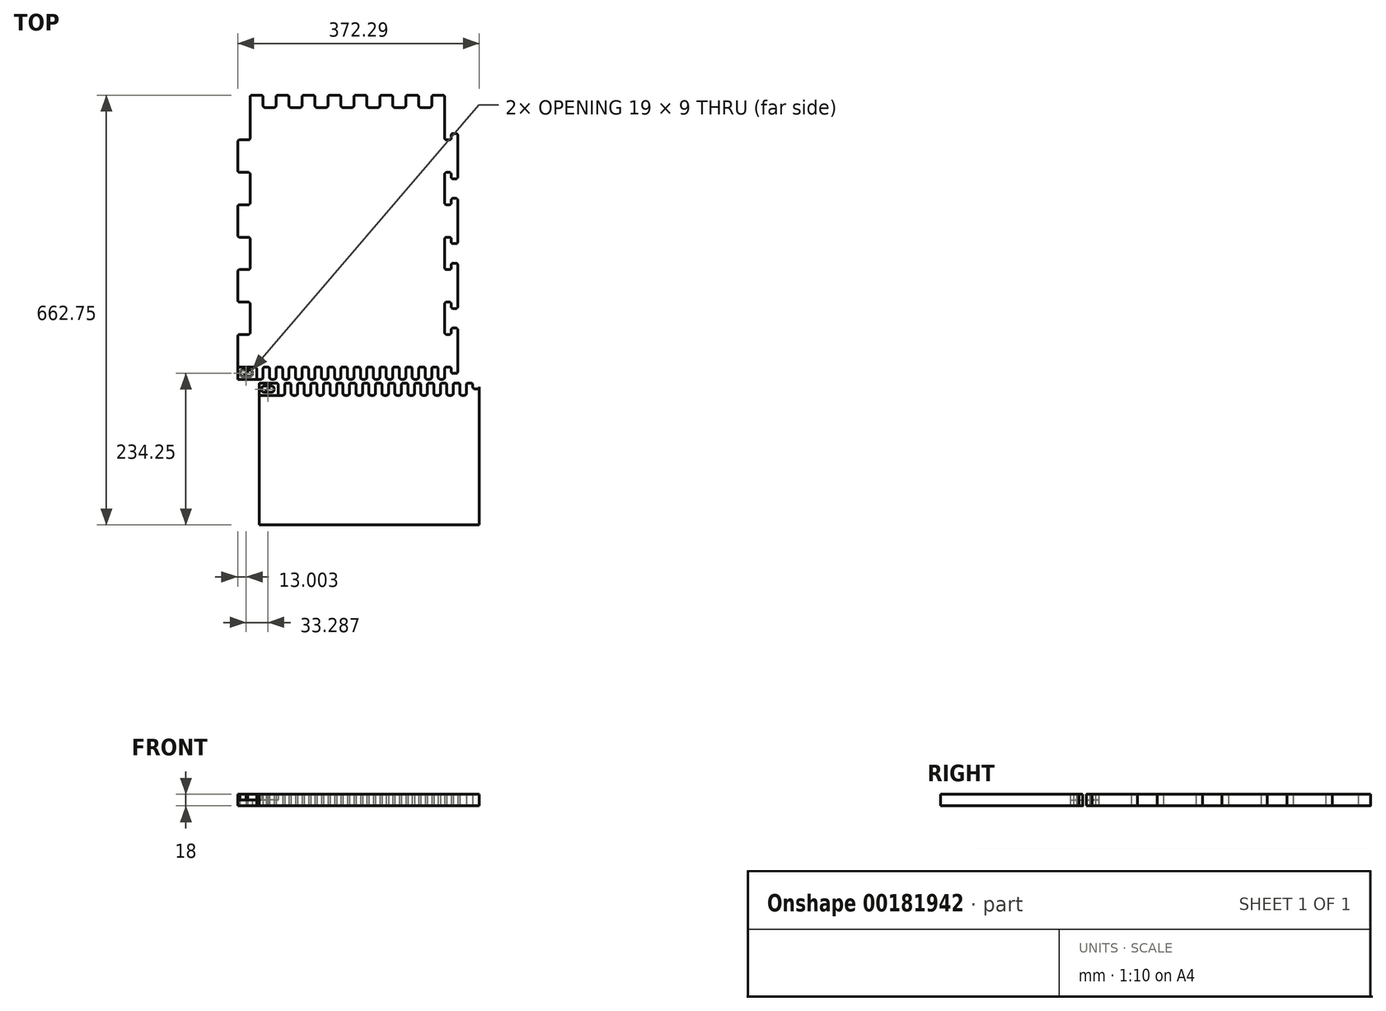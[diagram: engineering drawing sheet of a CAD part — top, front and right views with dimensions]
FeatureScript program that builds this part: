
annotation { "Feature Type Name" : "Feature", "Feature Type Description" : "" }
export const myFeature = defineFeature(function(context is Context, id is Id, definition is map)
    precondition{}
    {
        {
            var Q0;
            Q0=qCreatedBy(makeId("Top.planeOp"),FACE);
            var sketch = newSketch(context, id + "F0", { "sketchPlane" : qUnion([Q0])});
            skLineSegment(sketch, "E0.bottom", {"start": v(0, 0) * mm, "end": v(2000, 0) * mm, "construction": true});
            skLineSegment(sketch, "E0.top", {"start": v(0, 1000) * mm, "end": v(2000, 1000) * mm, "construction": true});
            skLineSegment(sketch, "E0.left", {"start": v(0, 0) * mm, "end": v(0, 1000) * mm, "construction": true});
            skLineSegment(sketch, "E0.right", {"start": v(2000, 0) * mm, "end": v(2000, 1000) * mm, "construction": true});
            skSolve(sketch);
        }
        {
            var Q0;
            Q0=qCreatedBy(makeId("Top.planeOp"),FACE);
            var sketch = newSketch(context, id + "F1", { "sketchPlane" : qUnion([Q0])});
            skLineSegment(sketch, "E1.bottom", {"start": v(5, 5) * mm, "end": v(1995, 5) * mm, "construction": true});
            skLineSegment(sketch, "E1.top", {"start": v(5, 995) * mm, "end": v(1995, 995) * mm, "construction": true});
            skLineSegment(sketch, "E1.left", {"start": v(5, 5) * mm, "end": v(5, 995) * mm, "construction": true});
            skLineSegment(sketch, "E1.right", {"start": v(1995, 5) * mm, "end": v(1995, 995) * mm, "construction": true});
            skPoint(sketch, "E2", {"position": v(0, 0) * mm});
            skPoint(sketch, "E3", {"position": v(5, 5) * mm});
            skSolve(sketch);
        }
        {
            var Q0;
            Q0=qCreatedBy(makeId("Top.planeOp"),FACE);
            var sketch = newSketch(context, id + "F2", { "sketchPlane" : qUnion([Q0])});
            skLineSegment(sketch, "E4.left", {"start": v(301.71, 681.75) * mm, "end": v(301.71, 728.75) * mm});
            skLineSegment(sketch, "E4.right", {"start": v(601.71, 681.75) * mm, "end": v(601.71, 728.75) * mm});
            skLineSegment(sketch, "E5.bottom", {"start": v(301.71, 728.75) * mm, "end": v(321.71, 728.75) * mm, "construction": true});
            skLineSegment(sketch, "E5.top", {"start": v(304.71, 747.75) * mm, "end": v(318.71, 747.75) * mm});
            skLineSegment(sketch, "E5.left", {"start": v(301.71, 728.75) * mm, "end": v(301.71, 744.75) * mm});
            skLineSegment(sketch, "E5.right", {"start": v(321.71, 731.75) * mm, "end": v(321.71, 744.75) * mm});
            skLineSegment(sketch, "E6.bottom", {"start": v(298.71, 678.75) * mm, "end": v(285.71, 678.75) * mm});
            skLineSegment(sketch, "E6.top", {"start": v(298.71, 628.75) * mm, "end": v(285.71, 628.75) * mm});
            skLineSegment(sketch, "E6.left", {"start": v(301.71, 678.75) * mm, "end": v(301.71, 628.75) * mm});
            skLineSegment(sketch, "E6.right", {"start": v(282.71, 675.75) * mm, "end": v(282.71, 631.75) * mm});
            skLineSegment(sketch, "E7.bottom", {"start": v(314.71, 309.75) * mm, "end": v(318.71, 309.75) * mm});
            skLineSegment(sketch, "E8.bottom", {"start": v(604.71, 678.75) * mm, "end": v(608.71, 678.75) * mm});
            skLineSegment(sketch, "E8.top", {"start": v(604.71, 628.75) * mm, "end": v(608.71, 628.75) * mm});
            skLineSegment(sketch, "E8.left", {"start": v(601.71, 678.75) * mm, "end": v(601.71, 628.75) * mm});
            skLineSegment(sketch, "E8.right", {"start": v(621.71, 678.75) * mm, "end": v(621.71, 628.75) * mm});
            skLineSegment(sketch, "E9.bottom", {"start": v(621.71, 678.75) * mm, "end": v(611.71, 678.75) * mm});
            skLineSegment(sketch, "E9.top", {"start": v(618.71, 688.75) * mm, "end": v(614.71, 688.75) * mm});
            skLineSegment(sketch, "E9.left", {"start": v(621.71, 678.75) * mm, "end": v(621.71, 685.75) * mm});
            skLineSegment(sketch, "E9.right", {"start": v(611.71, 681.75) * mm, "end": v(611.71, 685.75) * mm});
            skLineSegment(sketch, "E10.bottom", {"start": v(621.71, 628.75) * mm, "end": v(611.71, 628.75) * mm});
            skLineSegment(sketch, "E10.top", {"start": v(618.71, 618.75) * mm, "end": v(614.71, 618.75) * mm});
            skLineSegment(sketch, "E10.left", {"start": v(621.71, 628.75) * mm, "end": v(621.71, 621.75) * mm});
            skLineSegment(sketch, "E10.right", {"start": v(611.71, 625.75) * mm, "end": v(611.71, 621.75) * mm});
            skPoint(sketch, "E11.visualSharp", {"position": v(611.71, 688.75) * mm});
            skArc(sketch, "E11.filletArc", {"start": v(614.71, 688.75) * mm, "mid": v(612.6, 687.87) * mm, "end": v(611.71, 685.75) * mm});
            skPoint(sketch, "E12.visualSharp", {"position": v(621.71, 688.75) * mm});
            skArc(sketch, "E12.filletArc", {"start": v(621.71, 685.75) * mm, "mid": v(620.83, 687.87) * mm, "end": v(618.71, 688.75) * mm});
            skPoint(sketch, "E13.visualSharp", {"position": v(621.71, 618.75) * mm});
            skArc(sketch, "E13.filletArc", {"start": v(618.71, 618.75) * mm, "mid": v(620.83, 619.63) * mm, "end": v(621.71, 621.75) * mm});
            skPoint(sketch, "E14.visualSharp", {"position": v(611.71, 618.75) * mm});
            skArc(sketch, "E14.filletArc", {"start": v(611.71, 621.75) * mm, "mid": v(612.6, 619.63) * mm, "end": v(614.71, 618.75) * mm});
            skPoint(sketch, "E15.visualSharp", {"position": v(321.71, 747.75) * mm});
            skArc(sketch, "E15.filletArc", {"start": v(321.71, 744.75) * mm, "mid": v(320.83, 746.87) * mm, "end": v(318.71, 747.75) * mm});
            skPoint(sketch, "E16.visualSharp", {"position": v(301.71, 747.75) * mm});
            skArc(sketch, "E16.filletArc", {"start": v(304.71, 747.75) * mm, "mid": v(302.6, 746.87) * mm, "end": v(301.71, 744.75) * mm});
            skPoint(sketch, "E17.visualSharp", {"position": v(282.71, 678.75) * mm});
            skArc(sketch, "E17.filletArc", {"start": v(285.71, 678.75) * mm, "mid": v(283.6, 677.87) * mm, "end": v(282.71, 675.75) * mm});
            skPoint(sketch, "E18.visualSharp", {"position": v(282.71, 628.75) * mm});
            skArc(sketch, "E18.filletArc", {"start": v(282.71, 631.75) * mm, "mid": v(283.6, 629.63) * mm, "end": v(285.71, 628.75) * mm});
            skPoint(sketch, "E19.visualSharp", {"position": v(321.71, 309.75) * mm});
            skArc(sketch, "E19.filletArc", {"start": v(318.71, 309.75) * mm, "mid": v(320.83, 310.63) * mm, "end": v(321.71, 312.75) * mm});
            skPoint(sketch, "E20.visualSharp", {"position": v(311.71, 309.75) * mm});
            skArc(sketch, "E21.filletArc", {"start": v(608.71, 678.75) * mm, "mid": v(610.83, 679.63) * mm, "end": v(611.71, 681.75) * mm});
            skPoint(sketch, "E22.newPointB", {"position": v(621.71, 628.75) * mm});
            skArc(sketch, "E22.filletArc", {"start": v(611.71, 625.75) * mm, "mid": v(610.83, 627.87) * mm, "end": v(608.71, 628.75) * mm});
            skPoint(sketch, "E23.newPointA", {"position": v(301.71, 678.75) * mm});
            skPoint(sketch, "E23.newPointB", {"position": v(301.71, 328.75) * mm});
            skArc(sketch, "E23.filletArc", {"start": v(298.71, 678.75) * mm, "mid": v(300.83, 679.63) * mm, "end": v(301.71, 681.75) * mm});
            skLineSegment(sketch, "E24", {"start": v(301.71, 625.75) * mm, "end": v(301.71, 578.75) * mm});
            skPoint(sketch, "E25.visualSharp", {"position": v(301.71, 628.75) * mm});
            skArc(sketch, "E25.filletArc", {"start": v(301.71, 625.75) * mm, "mid": v(300.83, 627.87) * mm, "end": v(298.71, 628.75) * mm});
            skLineSegment(sketch, "E26.0.1.0", {"start": v(298.71, 578.75) * mm, "end": v(285.71, 578.75) * mm});
            skArc(sketch, "E26.0.1.1", {"start": v(298.71, 578.75) * mm, "mid": v(300.83, 579.63) * mm, "end": v(301.71, 581.75) * mm});
            skArc(sketch, "E26.0.1.2", {"start": v(285.71, 578.75) * mm, "mid": v(283.6, 577.87) * mm, "end": v(282.71, 575.75) * mm});
            skLineSegment(sketch, "E26.0.1.3", {"start": v(282.71, 575.75) * mm, "end": v(282.71, 531.75) * mm});
            skArc(sketch, "E26.0.1.4", {"start": v(282.71, 531.75) * mm, "mid": v(283.6, 529.63) * mm, "end": v(285.71, 528.75) * mm});
            skLineSegment(sketch, "E26.0.1.5", {"start": v(298.71, 528.75) * mm, "end": v(285.71, 528.75) * mm});
            skArc(sketch, "E26.0.1.6", {"start": v(301.71, 525.75) * mm, "mid": v(300.83, 527.87) * mm, "end": v(298.71, 528.75) * mm});
            skLineSegment(sketch, "E26.0.1.7", {"start": v(604.71, 578.75) * mm, "end": v(608.71, 578.75) * mm});
            skArc(sketch, "E26.0.1.8", {"start": v(608.71, 578.75) * mm, "mid": v(610.83, 579.63) * mm, "end": v(611.71, 581.75) * mm});
            skLineSegment(sketch, "E26.0.1.9", {"start": v(611.71, 581.75) * mm, "end": v(611.71, 585.75) * mm});
            skArc(sketch, "E26.0.1.10", {"start": v(614.71, 588.75) * mm, "mid": v(612.6, 587.87) * mm, "end": v(611.71, 585.75) * mm});
            skLineSegment(sketch, "E26.0.1.11", {"start": v(618.71, 588.75) * mm, "end": v(614.71, 588.75) * mm});
            skArc(sketch, "E26.0.1.12", {"start": v(621.71, 585.75) * mm, "mid": v(620.83, 587.87) * mm, "end": v(618.71, 588.75) * mm});
            skLineSegment(sketch, "E26.0.1.13", {"start": v(621.71, 578.75) * mm, "end": v(621.71, 585.75) * mm});
            skLineSegment(sketch, "E26.0.1.14", {"start": v(621.71, 578.75) * mm, "end": v(621.71, 528.75) * mm});
            skLineSegment(sketch, "E26.0.1.15", {"start": v(621.71, 578.75) * mm, "end": v(611.71, 578.75) * mm});
            skPoint(sketch, "E26.0.1.16", {"position": v(611.71, 588.75) * mm});
            skPoint(sketch, "E26.0.1.17", {"position": v(621.71, 588.75) * mm});
            skLineSegment(sketch, "E26.0.1.18", {"start": v(621.71, 528.75) * mm, "end": v(621.71, 521.75) * mm});
            skLineSegment(sketch, "E26.0.1.19", {"start": v(621.71, 528.75) * mm, "end": v(611.71, 528.75) * mm});
            skArc(sketch, "E26.0.1.20", {"start": v(618.71, 518.75) * mm, "mid": v(620.83, 519.63) * mm, "end": v(621.71, 521.75) * mm});
            skLineSegment(sketch, "E26.0.1.21", {"start": v(618.71, 518.75) * mm, "end": v(614.71, 518.75) * mm});
            skArc(sketch, "E26.0.1.22", {"start": v(611.71, 521.75) * mm, "mid": v(612.6, 519.63) * mm, "end": v(614.71, 518.75) * mm});
            skPoint(sketch, "E26.0.1.23", {"position": v(611.71, 518.75) * mm});
            skLineSegment(sketch, "E26.0.1.24", {"start": v(611.71, 525.75) * mm, "end": v(611.71, 521.75) * mm});
            skArc(sketch, "E26.0.1.25", {"start": v(611.71, 525.75) * mm, "mid": v(610.83, 527.87) * mm, "end": v(608.71, 528.75) * mm});
            skLineSegment(sketch, "E26.0.1.26", {"start": v(601.71, 528.75) * mm, "end": v(608.71, 528.75) * mm});
            skLineSegment(sketch, "E26.0.1.27", {"start": v(301.71, 578.75) * mm, "end": v(301.71, 528.75) * mm});
            skPoint(sketch, "E26.0.1.28", {"position": v(301.71, 578.75) * mm});
            skPoint(sketch, "E26.0.1.29", {"position": v(282.71, 578.75) * mm});
            skPoint(sketch, "E26.0.1.30", {"position": v(282.71, 528.75) * mm});
            skPoint(sketch, "E26.0.1.31", {"position": v(301.71, 528.75) * mm});
            skLineSegment(sketch, "E26.0.2.0", {"start": v(298.71, 478.75) * mm, "end": v(285.71, 478.75) * mm});
            skArc(sketch, "E26.0.2.1", {"start": v(298.71, 478.75) * mm, "mid": v(300.83, 479.63) * mm, "end": v(301.71, 481.75) * mm});
            skArc(sketch, "E26.0.2.2", {"start": v(285.71, 478.75) * mm, "mid": v(283.6, 477.87) * mm, "end": v(282.71, 475.75) * mm});
            skLineSegment(sketch, "E26.0.2.3", {"start": v(282.71, 475.75) * mm, "end": v(282.71, 431.75) * mm});
            skArc(sketch, "E26.0.2.4", {"start": v(282.71, 431.75) * mm, "mid": v(283.6, 429.63) * mm, "end": v(285.71, 428.75) * mm});
            skLineSegment(sketch, "E26.0.2.5", {"start": v(298.71, 428.75) * mm, "end": v(285.71, 428.75) * mm});
            skArc(sketch, "E26.0.2.6", {"start": v(301.71, 425.75) * mm, "mid": v(300.83, 427.87) * mm, "end": v(298.71, 428.75) * mm});
            skLineSegment(sketch, "E26.0.2.7", {"start": v(601.71, 478.75) * mm, "end": v(608.71, 478.75) * mm});
            skArc(sketch, "E26.0.2.8", {"start": v(608.71, 478.75) * mm, "mid": v(610.83, 479.63) * mm, "end": v(611.71, 481.75) * mm});
            skLineSegment(sketch, "E26.0.2.9", {"start": v(611.71, 481.75) * mm, "end": v(611.71, 485.75) * mm});
            skArc(sketch, "E26.0.2.10", {"start": v(614.71, 488.75) * mm, "mid": v(612.6, 487.87) * mm, "end": v(611.71, 485.75) * mm});
            skLineSegment(sketch, "E26.0.2.11", {"start": v(618.71, 488.75) * mm, "end": v(614.71, 488.75) * mm});
            skArc(sketch, "E26.0.2.12", {"start": v(621.71, 485.75) * mm, "mid": v(620.83, 487.87) * mm, "end": v(618.71, 488.75) * mm});
            skLineSegment(sketch, "E26.0.2.13", {"start": v(621.71, 478.75) * mm, "end": v(621.71, 485.75) * mm});
            skLineSegment(sketch, "E26.0.2.14", {"start": v(621.71, 478.75) * mm, "end": v(621.71, 428.75) * mm});
            skLineSegment(sketch, "E26.0.2.15", {"start": v(621.71, 478.75) * mm, "end": v(611.71, 478.75) * mm});
            skPoint(sketch, "E26.0.2.16", {"position": v(611.71, 488.75) * mm});
            skPoint(sketch, "E26.0.2.17", {"position": v(621.71, 488.75) * mm});
            skLineSegment(sketch, "E26.0.2.18", {"start": v(621.71, 428.75) * mm, "end": v(621.71, 421.75) * mm});
            skLineSegment(sketch, "E26.0.2.19", {"start": v(621.71, 428.75) * mm, "end": v(611.71, 428.75) * mm});
            skArc(sketch, "E26.0.2.20", {"start": v(618.71, 418.75) * mm, "mid": v(620.83, 419.63) * mm, "end": v(621.71, 421.75) * mm});
            skLineSegment(sketch, "E26.0.2.21", {"start": v(618.71, 418.75) * mm, "end": v(614.71, 418.75) * mm});
            skArc(sketch, "E26.0.2.22", {"start": v(611.71, 421.75) * mm, "mid": v(612.6, 419.63) * mm, "end": v(614.71, 418.75) * mm});
            skPoint(sketch, "E26.0.2.23", {"position": v(611.71, 418.75) * mm});
            skLineSegment(sketch, "E26.0.2.24", {"start": v(611.71, 425.75) * mm, "end": v(611.71, 421.75) * mm});
            skArc(sketch, "E26.0.2.25", {"start": v(611.71, 425.75) * mm, "mid": v(610.83, 427.87) * mm, "end": v(608.71, 428.75) * mm});
            skLineSegment(sketch, "E26.0.2.26", {"start": v(601.71, 428.75) * mm, "end": v(608.71, 428.75) * mm});
            skLineSegment(sketch, "E26.0.2.27", {"start": v(301.71, 478.75) * mm, "end": v(301.71, 428.75) * mm});
            skPoint(sketch, "E26.0.2.28", {"position": v(301.71, 478.75) * mm});
            skPoint(sketch, "E26.0.2.29", {"position": v(282.71, 478.75) * mm});
            skPoint(sketch, "E26.0.2.30", {"position": v(282.71, 428.75) * mm});
            skPoint(sketch, "E26.0.2.31", {"position": v(301.71, 428.75) * mm});
            skLineSegment(sketch, "E26.0.3.0", {"start": v(298.71, 378.75) * mm, "end": v(285.71, 378.75) * mm});
            skArc(sketch, "E26.0.3.1", {"start": v(298.71, 378.75) * mm, "mid": v(300.83, 379.63) * mm, "end": v(301.71, 381.75) * mm});
            skArc(sketch, "E26.0.3.2", {"start": v(285.71, 378.75) * mm, "mid": v(283.6, 377.87) * mm, "end": v(282.71, 375.75) * mm});
            skLineSegment(sketch, "E26.0.3.7", {"start": v(601.71, 378.75) * mm, "end": v(608.71, 378.75) * mm});
            skArc(sketch, "E26.0.3.8", {"start": v(608.71, 378.75) * mm, "mid": v(610.83, 379.63) * mm, "end": v(611.71, 381.75) * mm});
            skLineSegment(sketch, "E26.0.3.9", {"start": v(611.71, 381.75) * mm, "end": v(611.71, 385.75) * mm});
            skArc(sketch, "E26.0.3.10", {"start": v(614.71, 388.75) * mm, "mid": v(612.6, 387.87) * mm, "end": v(611.71, 385.75) * mm});
            skLineSegment(sketch, "E26.0.3.11", {"start": v(618.71, 388.75) * mm, "end": v(614.71, 388.75) * mm});
            skArc(sketch, "E26.0.3.12", {"start": v(621.71, 385.75) * mm, "mid": v(620.83, 387.87) * mm, "end": v(618.71, 388.75) * mm});
            skLineSegment(sketch, "E26.0.3.13", {"start": v(621.71, 378.75) * mm, "end": v(621.71, 385.75) * mm});
            skLineSegment(sketch, "E26.0.3.14", {"start": v(621.71, 378.75) * mm, "end": v(621.71, 328.75) * mm});
            skLineSegment(sketch, "E26.0.3.15", {"start": v(621.71, 378.75) * mm, "end": v(611.71, 378.75) * mm});
            skPoint(sketch, "E26.0.3.16", {"position": v(611.71, 388.75) * mm});
            skPoint(sketch, "E26.0.3.17", {"position": v(621.71, 388.75) * mm});
            skLineSegment(sketch, "E26.0.3.18", {"start": v(621.71, 328.75) * mm, "end": v(621.71, 321.75) * mm});
            skLineSegment(sketch, "E26.0.3.19", {"start": v(621.71, 328.75) * mm, "end": v(611.71, 328.75) * mm});
            skArc(sketch, "E26.0.3.20", {"start": v(618.71, 318.75) * mm, "mid": v(620.83, 319.63) * mm, "end": v(621.71, 321.75) * mm});
            skLineSegment(sketch, "E26.0.3.21", {"start": v(618.71, 318.75) * mm, "end": v(614.71, 318.75) * mm});
            skArc(sketch, "E26.0.3.22", {"start": v(611.71, 321.75) * mm, "mid": v(612.6, 319.63) * mm, "end": v(614.71, 318.75) * mm});
            skPoint(sketch, "E26.0.3.23", {"position": v(611.71, 318.75) * mm});
            skLineSegment(sketch, "E26.0.3.24", {"start": v(611.71, 325.75) * mm, "end": v(611.71, 321.75) * mm});
            skArc(sketch, "E26.0.3.25", {"start": v(611.71, 325.75) * mm, "mid": v(610.83, 327.87) * mm, "end": v(608.71, 328.75) * mm});
            skLineSegment(sketch, "E26.0.3.26", {"start": v(601.71, 328.75) * mm, "end": v(608.71, 328.75) * mm});
            skPoint(sketch, "E26.0.3.28", {"position": v(301.71, 378.75) * mm});
            skPoint(sketch, "E26.0.3.29", {"position": v(282.71, 378.75) * mm});
            skPoint(sketch, "E26.0.3.30", {"position": v(282.71, 328.75) * mm});
            skLineSegment(sketch, "E26.direction1", {"start": v(285.71, 678.75) * mm, "end": v(310.71, 678.75) * mm, "construction": true});
            skLineSegment(sketch, "E26.direction2", {"start": v(285.71, 678.75) * mm, "end": v(285.71, 578.75) * mm, "construction": true});
            skPoint(sketch, "E27.newPointA", {"position": v(601.71, 678.75) * mm});
            skArc(sketch, "E27.filletArc", {"start": v(601.71, 681.75) * mm, "mid": v(602.6, 679.63) * mm, "end": v(604.71, 678.75) * mm});
            skLineSegment(sketch, "E28", {"start": v(601.71, 625.75) * mm, "end": v(601.71, 581.75) * mm});
            skPoint(sketch, "E29.visualSharp", {"position": v(601.71, 628.75) * mm});
            skArc(sketch, "E29.filletArc", {"start": v(604.71, 628.75) * mm, "mid": v(602.6, 627.87) * mm, "end": v(601.71, 625.75) * mm});
            skPoint(sketch, "E30.visualSharp", {"position": v(601.71, 578.75) * mm});
            skArc(sketch, "E30.filletArc", {"start": v(601.71, 581.75) * mm, "mid": v(602.6, 579.63) * mm, "end": v(604.71, 578.75) * mm});
            skLineSegment(sketch, "E31.0.1.0", {"start": v(604.71, 528.75) * mm, "end": v(608.71, 528.75) * mm});
            skLineSegment(sketch, "E31.0.1.1", {"start": v(604.71, 478.75) * mm, "end": v(608.71, 478.75) * mm});
            skArc(sketch, "E31.0.1.2", {"start": v(604.71, 528.75) * mm, "mid": v(602.6, 527.87) * mm, "end": v(601.71, 525.75) * mm});
            skArc(sketch, "E31.0.1.3", {"start": v(601.71, 481.75) * mm, "mid": v(602.6, 479.63) * mm, "end": v(604.71, 478.75) * mm});
            skPoint(sketch, "E31.0.1.4", {"position": v(601.71, 478.75) * mm});
            skPoint(sketch, "E31.0.1.5", {"position": v(601.71, 528.75) * mm});
            skLineSegment(sketch, "E31.0.1.6", {"start": v(601.71, 525.75) * mm, "end": v(601.71, 481.75) * mm});
            skLineSegment(sketch, "E31.0.2.0", {"start": v(604.71, 428.75) * mm, "end": v(608.71, 428.75) * mm});
            skLineSegment(sketch, "E31.0.2.1", {"start": v(604.71, 378.75) * mm, "end": v(608.71, 378.75) * mm});
            skArc(sketch, "E31.0.2.2", {"start": v(604.71, 428.75) * mm, "mid": v(602.6, 427.87) * mm, "end": v(601.71, 425.75) * mm});
            skArc(sketch, "E31.0.2.3", {"start": v(601.71, 381.75) * mm, "mid": v(602.6, 379.63) * mm, "end": v(604.71, 378.75) * mm});
            skPoint(sketch, "E31.0.2.4", {"position": v(601.71, 378.75) * mm});
            skPoint(sketch, "E31.0.2.5", {"position": v(601.71, 428.75) * mm});
            skLineSegment(sketch, "E31.0.2.6", {"start": v(601.71, 425.75) * mm, "end": v(601.71, 381.75) * mm});
            skLineSegment(sketch, "E31.0.3.0", {"start": v(604.71, 328.75) * mm, "end": v(608.71, 328.75) * mm});
            skPoint(sketch, "E31.0.3.5", {"position": v(601.71, 328.75) * mm});
            skLineSegment(sketch, "E31.direction1", {"start": v(604.71, 628.75) * mm, "end": v(629.71, 628.75) * mm, "construction": true});
            skLineSegment(sketch, "E31.direction2", {"start": v(604.71, 628.75) * mm, "end": v(604.71, 528.75) * mm, "construction": true});
            skLineSegment(sketch, "E32", {"start": v(301.71, 381.75) * mm, "end": v(301.71, 425.75) * mm});
            skLineSegment(sketch, "E33", {"start": v(301.71, 481.75) * mm, "end": v(301.71, 525.75) * mm});
            skLineSegment(sketch, "E34", {"start": v(298.71, 328.75) * mm, "end": v(308.71, 328.75) * mm});
            skPoint(sketch, "E35.visualSharp", {"position": v(311.71, 328.75) * mm});
            skArc(sketch, "E35.filletArc", {"start": v(311.71, 325.75) * mm, "mid": v(310.83, 327.87) * mm, "end": v(308.71, 328.75) * mm});
            skLineSegment(sketch, "E36", {"start": v(321.71, 325.75) * mm, "end": v(321.71, 312.75) * mm});
            skLineSegment(sketch, "E37", {"start": v(324.71, 328.75) * mm, "end": v(328.71, 328.75) * mm});
            skPoint(sketch, "E38.visualSharp", {"position": v(321.71, 328.75) * mm});
            skArc(sketch, "E38.filletArc", {"start": v(324.71, 328.75) * mm, "mid": v(322.6, 327.87) * mm, "end": v(321.71, 325.75) * mm});
            skPoint(sketch, "E39.visualSharp", {"position": v(331.71, 328.75) * mm});
            skArc(sketch, "E39.filletArc", {"start": v(331.71, 325.75) * mm, "mid": v(330.83, 327.87) * mm, "end": v(328.71, 328.75) * mm});
            skLineSegment(sketch, "E40.1.0.0", {"start": v(331.71, 312.75) * mm, "end": v(331.71, 325.75) * mm});
            skLineSegment(sketch, "E40.1.0.1", {"start": v(341.71, 325.75) * mm, "end": v(341.71, 312.75) * mm});
            skLineSegment(sketch, "E40.1.0.2", {"start": v(344.71, 328.75) * mm, "end": v(348.71, 328.75) * mm});
            skArc(sketch, "E40.1.0.3", {"start": v(344.71, 328.75) * mm, "mid": v(342.6, 327.87) * mm, "end": v(341.71, 325.75) * mm});
            skLineSegment(sketch, "E40.1.0.5", {"start": v(334.71, 309.75) * mm, "end": v(338.71, 309.75) * mm});
            skArc(sketch, "E40.1.0.6", {"start": v(338.71, 309.75) * mm, "mid": v(340.83, 310.63) * mm, "end": v(341.71, 312.75) * mm});
            skArc(sketch, "E40.1.0.7", {"start": v(331.71, 312.75) * mm, "mid": v(332.6, 310.63) * mm, "end": v(334.71, 309.75) * mm});
            skArc(sketch, "E40.1.0.8", {"start": v(351.71, 325.75) * mm, "mid": v(350.83, 327.87) * mm, "end": v(348.71, 328.75) * mm});
            skPoint(sketch, "E40.1.0.9", {"position": v(341.71, 328.75) * mm});
            skPoint(sketch, "E40.1.0.10", {"position": v(351.71, 328.75) * mm});
            skPoint(sketch, "E40.1.0.12", {"position": v(331.71, 309.75) * mm});
            skPoint(sketch, "E40.1.0.13", {"position": v(341.71, 309.75) * mm});
            skLineSegment(sketch, "E40.2.0.0", {"start": v(351.71, 312.75) * mm, "end": v(351.71, 325.75) * mm});
            skLineSegment(sketch, "E40.2.0.1", {"start": v(361.71, 325.75) * mm, "end": v(361.71, 312.75) * mm});
            skLineSegment(sketch, "E40.2.0.2", {"start": v(364.71, 328.75) * mm, "end": v(368.71, 328.75) * mm});
            skArc(sketch, "E40.2.0.3", {"start": v(364.71, 328.75) * mm, "mid": v(362.6, 327.87) * mm, "end": v(361.71, 325.75) * mm});
            skArc(sketch, "E40.2.0.4", {"start": v(351.71, 325.75) * mm, "mid": v(350.83, 327.87) * mm, "end": v(348.71, 328.75) * mm});
            skLineSegment(sketch, "E40.2.0.5", {"start": v(354.71, 309.75) * mm, "end": v(358.71, 309.75) * mm});
            skArc(sketch, "E40.2.0.6", {"start": v(358.71, 309.75) * mm, "mid": v(360.83, 310.63) * mm, "end": v(361.71, 312.75) * mm});
            skArc(sketch, "E40.2.0.7", {"start": v(351.71, 312.75) * mm, "mid": v(352.6, 310.63) * mm, "end": v(354.71, 309.75) * mm});
            skArc(sketch, "E40.2.0.8", {"start": v(371.71, 325.75) * mm, "mid": v(370.83, 327.87) * mm, "end": v(368.71, 328.75) * mm});
            skPoint(sketch, "E40.2.0.9", {"position": v(361.71, 328.75) * mm});
            skPoint(sketch, "E40.2.0.10", {"position": v(371.71, 328.75) * mm});
            skPoint(sketch, "E40.2.0.11", {"position": v(351.71, 328.75) * mm});
            skPoint(sketch, "E40.2.0.12", {"position": v(351.71, 309.75) * mm});
            skPoint(sketch, "E40.2.0.13", {"position": v(361.71, 309.75) * mm});
            skLineSegment(sketch, "E40.3.0.0", {"start": v(371.71, 312.75) * mm, "end": v(371.71, 325.75) * mm});
            skLineSegment(sketch, "E40.3.0.1", {"start": v(381.71, 325.75) * mm, "end": v(381.71, 312.75) * mm});
            skLineSegment(sketch, "E40.3.0.2", {"start": v(384.71, 328.75) * mm, "end": v(388.71, 328.75) * mm});
            skArc(sketch, "E40.3.0.3", {"start": v(384.71, 328.75) * mm, "mid": v(382.6, 327.87) * mm, "end": v(381.71, 325.75) * mm});
            skArc(sketch, "E40.3.0.4", {"start": v(371.71, 325.75) * mm, "mid": v(370.83, 327.87) * mm, "end": v(368.71, 328.75) * mm});
            skLineSegment(sketch, "E40.3.0.5", {"start": v(374.71, 309.75) * mm, "end": v(378.71, 309.75) * mm});
            skArc(sketch, "E40.3.0.6", {"start": v(378.71, 309.75) * mm, "mid": v(380.83, 310.63) * mm, "end": v(381.71, 312.75) * mm});
            skArc(sketch, "E40.3.0.7", {"start": v(371.71, 312.75) * mm, "mid": v(372.6, 310.63) * mm, "end": v(374.71, 309.75) * mm});
            skArc(sketch, "E40.3.0.8", {"start": v(391.71, 325.75) * mm, "mid": v(390.83, 327.87) * mm, "end": v(388.71, 328.75) * mm});
            skPoint(sketch, "E40.3.0.9", {"position": v(381.71, 328.75) * mm});
            skPoint(sketch, "E40.3.0.10", {"position": v(391.71, 328.75) * mm});
            skPoint(sketch, "E40.3.0.11", {"position": v(371.71, 328.75) * mm});
            skPoint(sketch, "E40.3.0.12", {"position": v(371.71, 309.75) * mm});
            skPoint(sketch, "E40.3.0.13", {"position": v(381.71, 309.75) * mm});
            skLineSegment(sketch, "E40.4.0.0", {"start": v(391.71, 312.75) * mm, "end": v(391.71, 325.75) * mm});
            skLineSegment(sketch, "E40.4.0.1", {"start": v(401.71, 325.75) * mm, "end": v(401.71, 312.75) * mm});
            skLineSegment(sketch, "E40.4.0.2", {"start": v(404.71, 328.75) * mm, "end": v(408.71, 328.75) * mm});
            skArc(sketch, "E40.4.0.3", {"start": v(404.71, 328.75) * mm, "mid": v(402.6, 327.87) * mm, "end": v(401.71, 325.75) * mm});
            skArc(sketch, "E40.4.0.4", {"start": v(391.71, 325.75) * mm, "mid": v(390.83, 327.87) * mm, "end": v(388.71, 328.75) * mm});
            skLineSegment(sketch, "E40.4.0.5", {"start": v(394.71, 309.75) * mm, "end": v(398.71, 309.75) * mm});
            skArc(sketch, "E40.4.0.6", {"start": v(398.71, 309.75) * mm, "mid": v(400.83, 310.63) * mm, "end": v(401.71, 312.75) * mm});
            skArc(sketch, "E40.4.0.7", {"start": v(391.71, 312.75) * mm, "mid": v(392.6, 310.63) * mm, "end": v(394.71, 309.75) * mm});
            skArc(sketch, "E40.4.0.8", {"start": v(411.71, 325.75) * mm, "mid": v(410.83, 327.87) * mm, "end": v(408.71, 328.75) * mm});
            skPoint(sketch, "E40.4.0.9", {"position": v(401.71, 328.75) * mm});
            skPoint(sketch, "E40.4.0.10", {"position": v(411.71, 328.75) * mm});
            skPoint(sketch, "E40.4.0.11", {"position": v(391.71, 328.75) * mm});
            skPoint(sketch, "E40.4.0.12", {"position": v(391.71, 309.75) * mm});
            skPoint(sketch, "E40.4.0.13", {"position": v(401.71, 309.75) * mm});
            skLineSegment(sketch, "E40.5.0.0", {"start": v(411.71, 312.75) * mm, "end": v(411.71, 325.75) * mm});
            skLineSegment(sketch, "E40.5.0.1", {"start": v(421.71, 325.75) * mm, "end": v(421.71, 312.75) * mm});
            skLineSegment(sketch, "E40.5.0.2", {"start": v(424.71, 328.75) * mm, "end": v(428.71, 328.75) * mm});
            skArc(sketch, "E40.5.0.3", {"start": v(424.71, 328.75) * mm, "mid": v(422.6, 327.87) * mm, "end": v(421.71, 325.75) * mm});
            skArc(sketch, "E40.5.0.4", {"start": v(411.71, 325.75) * mm, "mid": v(410.83, 327.87) * mm, "end": v(408.71, 328.75) * mm});
            skLineSegment(sketch, "E40.5.0.5", {"start": v(414.71, 309.75) * mm, "end": v(418.71, 309.75) * mm});
            skArc(sketch, "E40.5.0.6", {"start": v(418.71, 309.75) * mm, "mid": v(420.83, 310.63) * mm, "end": v(421.71, 312.75) * mm});
            skArc(sketch, "E40.5.0.7", {"start": v(411.71, 312.75) * mm, "mid": v(412.6, 310.63) * mm, "end": v(414.71, 309.75) * mm});
            skArc(sketch, "E40.5.0.8", {"start": v(431.71, 325.75) * mm, "mid": v(430.83, 327.87) * mm, "end": v(428.71, 328.75) * mm});
            skPoint(sketch, "E40.5.0.9", {"position": v(421.71, 328.75) * mm});
            skPoint(sketch, "E40.5.0.10", {"position": v(431.71, 328.75) * mm});
            skPoint(sketch, "E40.5.0.11", {"position": v(411.71, 328.75) * mm});
            skPoint(sketch, "E40.5.0.12", {"position": v(411.71, 309.75) * mm});
            skPoint(sketch, "E40.5.0.13", {"position": v(421.71, 309.75) * mm});
            skLineSegment(sketch, "E40.6.0.0", {"start": v(431.71, 312.75) * mm, "end": v(431.71, 325.75) * mm});
            skLineSegment(sketch, "E40.6.0.1", {"start": v(441.71, 325.75) * mm, "end": v(441.71, 312.75) * mm});
            skLineSegment(sketch, "E40.6.0.2", {"start": v(444.71, 328.75) * mm, "end": v(448.71, 328.75) * mm});
            skArc(sketch, "E40.6.0.3", {"start": v(444.71, 328.75) * mm, "mid": v(442.6, 327.87) * mm, "end": v(441.71, 325.75) * mm});
            skArc(sketch, "E40.6.0.4", {"start": v(431.71, 325.75) * mm, "mid": v(430.83, 327.87) * mm, "end": v(428.71, 328.75) * mm});
            skLineSegment(sketch, "E40.6.0.5", {"start": v(434.71, 309.75) * mm, "end": v(438.71, 309.75) * mm});
            skArc(sketch, "E40.6.0.6", {"start": v(438.71, 309.75) * mm, "mid": v(440.83, 310.63) * mm, "end": v(441.71, 312.75) * mm});
            skArc(sketch, "E40.6.0.7", {"start": v(431.71, 312.75) * mm, "mid": v(432.6, 310.63) * mm, "end": v(434.71, 309.75) * mm});
            skArc(sketch, "E40.6.0.8", {"start": v(451.71, 325.75) * mm, "mid": v(450.83, 327.87) * mm, "end": v(448.71, 328.75) * mm});
            skPoint(sketch, "E40.6.0.9", {"position": v(441.71, 328.75) * mm});
            skPoint(sketch, "E40.6.0.10", {"position": v(451.71, 328.75) * mm});
            skPoint(sketch, "E40.6.0.11", {"position": v(431.71, 328.75) * mm});
            skPoint(sketch, "E40.6.0.12", {"position": v(431.71, 309.75) * mm});
            skPoint(sketch, "E40.6.0.13", {"position": v(441.71, 309.75) * mm});
            skLineSegment(sketch, "E40.7.0.0", {"start": v(451.71, 312.75) * mm, "end": v(451.71, 325.75) * mm});
            skLineSegment(sketch, "E40.7.0.1", {"start": v(461.71, 325.75) * mm, "end": v(461.71, 312.75) * mm});
            skLineSegment(sketch, "E40.7.0.2", {"start": v(464.71, 328.75) * mm, "end": v(468.71, 328.75) * mm});
            skArc(sketch, "E40.7.0.3", {"start": v(464.71, 328.75) * mm, "mid": v(462.6, 327.87) * mm, "end": v(461.71, 325.75) * mm});
            skArc(sketch, "E40.7.0.4", {"start": v(451.71, 325.75) * mm, "mid": v(450.83, 327.87) * mm, "end": v(448.71, 328.75) * mm});
            skLineSegment(sketch, "E40.7.0.5", {"start": v(454.71, 309.75) * mm, "end": v(458.71, 309.75) * mm});
            skArc(sketch, "E40.7.0.6", {"start": v(458.71, 309.75) * mm, "mid": v(460.83, 310.63) * mm, "end": v(461.71, 312.75) * mm});
            skArc(sketch, "E40.7.0.7", {"start": v(451.71, 312.75) * mm, "mid": v(452.6, 310.63) * mm, "end": v(454.71, 309.75) * mm});
            skArc(sketch, "E40.7.0.8", {"start": v(471.71, 325.75) * mm, "mid": v(470.83, 327.87) * mm, "end": v(468.71, 328.75) * mm});
            skPoint(sketch, "E40.7.0.9", {"position": v(461.71, 328.75) * mm});
            skPoint(sketch, "E40.7.0.10", {"position": v(471.71, 328.75) * mm});
            skPoint(sketch, "E40.7.0.11", {"position": v(451.71, 328.75) * mm});
            skPoint(sketch, "E40.7.0.12", {"position": v(451.71, 309.75) * mm});
            skPoint(sketch, "E40.7.0.13", {"position": v(461.71, 309.75) * mm});
            skLineSegment(sketch, "E40.8.0.0", {"start": v(471.71, 312.75) * mm, "end": v(471.71, 325.75) * mm});
            skLineSegment(sketch, "E40.8.0.1", {"start": v(481.71, 325.75) * mm, "end": v(481.71, 312.75) * mm});
            skLineSegment(sketch, "E40.8.0.2", {"start": v(484.71, 328.75) * mm, "end": v(488.71, 328.75) * mm});
            skArc(sketch, "E40.8.0.3", {"start": v(484.71, 328.75) * mm, "mid": v(482.6, 327.87) * mm, "end": v(481.71, 325.75) * mm});
            skArc(sketch, "E40.8.0.4", {"start": v(471.71, 325.75) * mm, "mid": v(470.83, 327.87) * mm, "end": v(468.71, 328.75) * mm});
            skLineSegment(sketch, "E40.8.0.5", {"start": v(474.71, 309.75) * mm, "end": v(478.71, 309.75) * mm});
            skArc(sketch, "E40.8.0.6", {"start": v(478.71, 309.75) * mm, "mid": v(480.83, 310.63) * mm, "end": v(481.71, 312.75) * mm});
            skArc(sketch, "E40.8.0.7", {"start": v(471.71, 312.75) * mm, "mid": v(472.6, 310.63) * mm, "end": v(474.71, 309.75) * mm});
            skArc(sketch, "E40.8.0.8", {"start": v(491.71, 325.75) * mm, "mid": v(490.83, 327.87) * mm, "end": v(488.71, 328.75) * mm});
            skPoint(sketch, "E40.8.0.9", {"position": v(481.71, 328.75) * mm});
            skPoint(sketch, "E40.8.0.10", {"position": v(491.71, 328.75) * mm});
            skPoint(sketch, "E40.8.0.11", {"position": v(471.71, 328.75) * mm});
            skPoint(sketch, "E40.8.0.12", {"position": v(471.71, 309.75) * mm});
            skPoint(sketch, "E40.8.0.13", {"position": v(481.71, 309.75) * mm});
            skLineSegment(sketch, "E40.9.0.0", {"start": v(491.71, 312.75) * mm, "end": v(491.71, 325.75) * mm});
            skLineSegment(sketch, "E40.9.0.1", {"start": v(501.71, 325.75) * mm, "end": v(501.71, 312.75) * mm});
            skLineSegment(sketch, "E40.9.0.2", {"start": v(504.71, 328.75) * mm, "end": v(508.71, 328.75) * mm});
            skArc(sketch, "E40.9.0.3", {"start": v(504.71, 328.75) * mm, "mid": v(502.6, 327.87) * mm, "end": v(501.71, 325.75) * mm});
            skArc(sketch, "E40.9.0.4", {"start": v(491.71, 325.75) * mm, "mid": v(490.83, 327.87) * mm, "end": v(488.71, 328.75) * mm});
            skLineSegment(sketch, "E40.9.0.5", {"start": v(494.71, 309.75) * mm, "end": v(498.71, 309.75) * mm});
            skArc(sketch, "E40.9.0.6", {"start": v(498.71, 309.75) * mm, "mid": v(500.83, 310.63) * mm, "end": v(501.71, 312.75) * mm});
            skArc(sketch, "E40.9.0.7", {"start": v(491.71, 312.75) * mm, "mid": v(492.6, 310.63) * mm, "end": v(494.71, 309.75) * mm});
            skArc(sketch, "E40.9.0.8", {"start": v(511.71, 325.75) * mm, "mid": v(510.83, 327.87) * mm, "end": v(508.71, 328.75) * mm});
            skPoint(sketch, "E40.9.0.9", {"position": v(501.71, 328.75) * mm});
            skPoint(sketch, "E40.9.0.10", {"position": v(511.71, 328.75) * mm});
            skPoint(sketch, "E40.9.0.11", {"position": v(491.71, 328.75) * mm});
            skPoint(sketch, "E40.9.0.12", {"position": v(491.71, 309.75) * mm});
            skPoint(sketch, "E40.9.0.13", {"position": v(501.71, 309.75) * mm});
            skLineSegment(sketch, "E40.10.0.0", {"start": v(511.71, 312.75) * mm, "end": v(511.71, 325.75) * mm});
            skLineSegment(sketch, "E40.10.0.1", {"start": v(521.71, 325.75) * mm, "end": v(521.71, 312.75) * mm});
            skLineSegment(sketch, "E40.10.0.2", {"start": v(524.71, 328.75) * mm, "end": v(528.71, 328.75) * mm});
            skArc(sketch, "E40.10.0.3", {"start": v(524.71, 328.75) * mm, "mid": v(522.6, 327.87) * mm, "end": v(521.71, 325.75) * mm});
            skArc(sketch, "E40.10.0.4", {"start": v(511.71, 325.75) * mm, "mid": v(510.83, 327.87) * mm, "end": v(508.71, 328.75) * mm});
            skLineSegment(sketch, "E40.10.0.5", {"start": v(514.71, 309.75) * mm, "end": v(518.71, 309.75) * mm});
            skArc(sketch, "E40.10.0.6", {"start": v(518.71, 309.75) * mm, "mid": v(520.83, 310.63) * mm, "end": v(521.71, 312.75) * mm});
            skArc(sketch, "E40.10.0.7", {"start": v(511.71, 312.75) * mm, "mid": v(512.6, 310.63) * mm, "end": v(514.71, 309.75) * mm});
            skArc(sketch, "E40.10.0.8", {"start": v(531.71, 325.75) * mm, "mid": v(530.83, 327.87) * mm, "end": v(528.71, 328.75) * mm});
            skPoint(sketch, "E40.10.0.9", {"position": v(521.71, 328.75) * mm});
            skPoint(sketch, "E40.10.0.10", {"position": v(531.71, 328.75) * mm});
            skPoint(sketch, "E40.10.0.11", {"position": v(511.71, 328.75) * mm});
            skPoint(sketch, "E40.10.0.12", {"position": v(511.71, 309.75) * mm});
            skPoint(sketch, "E40.10.0.13", {"position": v(521.71, 309.75) * mm});
            skLineSegment(sketch, "E40.11.0.0", {"start": v(531.71, 312.75) * mm, "end": v(531.71, 325.75) * mm});
            skLineSegment(sketch, "E40.11.0.1", {"start": v(541.71, 325.75) * mm, "end": v(541.71, 312.75) * mm});
            skLineSegment(sketch, "E40.11.0.2", {"start": v(544.71, 328.75) * mm, "end": v(548.71, 328.75) * mm});
            skArc(sketch, "E40.11.0.3", {"start": v(544.71, 328.75) * mm, "mid": v(542.6, 327.87) * mm, "end": v(541.71, 325.75) * mm});
            skArc(sketch, "E40.11.0.4", {"start": v(531.71, 325.75) * mm, "mid": v(530.83, 327.87) * mm, "end": v(528.71, 328.75) * mm});
            skLineSegment(sketch, "E40.11.0.5", {"start": v(534.71, 309.75) * mm, "end": v(538.71, 309.75) * mm});
            skArc(sketch, "E40.11.0.6", {"start": v(538.71, 309.75) * mm, "mid": v(540.83, 310.63) * mm, "end": v(541.71, 312.75) * mm});
            skArc(sketch, "E40.11.0.7", {"start": v(531.71, 312.75) * mm, "mid": v(532.6, 310.63) * mm, "end": v(534.71, 309.75) * mm});
            skArc(sketch, "E40.11.0.8", {"start": v(551.71, 325.75) * mm, "mid": v(550.83, 327.87) * mm, "end": v(548.71, 328.75) * mm});
            skPoint(sketch, "E40.11.0.9", {"position": v(541.71, 328.75) * mm});
            skPoint(sketch, "E40.11.0.10", {"position": v(551.71, 328.75) * mm});
            skPoint(sketch, "E40.11.0.11", {"position": v(531.71, 328.75) * mm});
            skPoint(sketch, "E40.11.0.12", {"position": v(531.71, 309.75) * mm});
            skPoint(sketch, "E40.11.0.13", {"position": v(541.71, 309.75) * mm});
            skLineSegment(sketch, "E40.12.0.0", {"start": v(551.71, 312.75) * mm, "end": v(551.71, 325.75) * mm});
            skLineSegment(sketch, "E40.12.0.1", {"start": v(561.71, 325.75) * mm, "end": v(561.71, 312.75) * mm});
            skLineSegment(sketch, "E40.12.0.2", {"start": v(564.71, 328.75) * mm, "end": v(568.71, 328.75) * mm});
            skArc(sketch, "E40.12.0.3", {"start": v(564.71, 328.75) * mm, "mid": v(562.6, 327.87) * mm, "end": v(561.71, 325.75) * mm});
            skArc(sketch, "E40.12.0.4", {"start": v(551.71, 325.75) * mm, "mid": v(550.83, 327.87) * mm, "end": v(548.71, 328.75) * mm});
            skLineSegment(sketch, "E40.12.0.5", {"start": v(554.71, 309.75) * mm, "end": v(558.71, 309.75) * mm});
            skArc(sketch, "E40.12.0.6", {"start": v(558.71, 309.75) * mm, "mid": v(560.83, 310.63) * mm, "end": v(561.71, 312.75) * mm});
            skArc(sketch, "E40.12.0.7", {"start": v(551.71, 312.75) * mm, "mid": v(552.6, 310.63) * mm, "end": v(554.71, 309.75) * mm});
            skArc(sketch, "E40.12.0.8", {"start": v(571.71, 325.75) * mm, "mid": v(570.83, 327.87) * mm, "end": v(568.71, 328.75) * mm});
            skPoint(sketch, "E40.12.0.9", {"position": v(561.71, 328.75) * mm});
            skPoint(sketch, "E40.12.0.10", {"position": v(571.71, 328.75) * mm});
            skPoint(sketch, "E40.12.0.11", {"position": v(551.71, 328.75) * mm});
            skPoint(sketch, "E40.12.0.12", {"position": v(551.71, 309.75) * mm});
            skPoint(sketch, "E40.12.0.13", {"position": v(561.71, 309.75) * mm});
            skLineSegment(sketch, "E40.13.0.0", {"start": v(571.71, 312.75) * mm, "end": v(571.71, 325.75) * mm});
            skLineSegment(sketch, "E40.13.0.1", {"start": v(581.71, 325.75) * mm, "end": v(581.71, 312.75) * mm});
            skLineSegment(sketch, "E40.13.0.2", {"start": v(584.71, 328.75) * mm, "end": v(588.71, 328.75) * mm});
            skArc(sketch, "E40.13.0.3", {"start": v(584.71, 328.75) * mm, "mid": v(582.6, 327.87) * mm, "end": v(581.71, 325.75) * mm});
            skArc(sketch, "E40.13.0.4", {"start": v(571.71, 325.75) * mm, "mid": v(570.83, 327.87) * mm, "end": v(568.71, 328.75) * mm});
            skLineSegment(sketch, "E40.13.0.5", {"start": v(574.71, 309.75) * mm, "end": v(578.71, 309.75) * mm});
            skArc(sketch, "E40.13.0.6", {"start": v(578.71, 309.75) * mm, "mid": v(580.83, 310.63) * mm, "end": v(581.71, 312.75) * mm});
            skArc(sketch, "E40.13.0.7", {"start": v(571.71, 312.75) * mm, "mid": v(572.6, 310.63) * mm, "end": v(574.71, 309.75) * mm});
            skArc(sketch, "E40.13.0.8", {"start": v(591.71, 325.75) * mm, "mid": v(590.83, 327.87) * mm, "end": v(588.71, 328.75) * mm});
            skPoint(sketch, "E40.13.0.9", {"position": v(581.71, 328.75) * mm});
            skPoint(sketch, "E40.13.0.10", {"position": v(591.71, 328.75) * mm});
            skPoint(sketch, "E40.13.0.11", {"position": v(571.71, 328.75) * mm});
            skPoint(sketch, "E40.13.0.12", {"position": v(571.71, 309.75) * mm});
            skPoint(sketch, "E40.13.0.13", {"position": v(581.71, 309.75) * mm});
            skLineSegment(sketch, "E40.14.0.0", {"start": v(591.71, 312.75) * mm, "end": v(591.71, 325.75) * mm});
            skLineSegment(sketch, "E40.14.0.1", {"start": v(601.71, 325.75) * mm, "end": v(601.71, 312.75) * mm});
            skArc(sketch, "E40.14.0.3", {"start": v(604.71, 328.75) * mm, "mid": v(602.6, 327.87) * mm, "end": v(601.71, 325.75) * mm});
            skArc(sketch, "E40.14.0.4", {"start": v(591.71, 325.75) * mm, "mid": v(590.83, 327.87) * mm, "end": v(588.71, 328.75) * mm});
            skLineSegment(sketch, "E40.14.0.5", {"start": v(594.71, 309.75) * mm, "end": v(598.71, 309.75) * mm});
            skArc(sketch, "E40.14.0.6", {"start": v(598.71, 309.75) * mm, "mid": v(600.83, 310.63) * mm, "end": v(601.71, 312.75) * mm});
            skArc(sketch, "E40.14.0.7", {"start": v(591.71, 312.75) * mm, "mid": v(592.6, 310.63) * mm, "end": v(594.71, 309.75) * mm});
            skPoint(sketch, "E40.14.0.10", {"position": v(611.71, 328.75) * mm});
            skPoint(sketch, "E40.14.0.11", {"position": v(591.71, 328.75) * mm});
            skPoint(sketch, "E40.14.0.12", {"position": v(591.71, 309.75) * mm});
            skPoint(sketch, "E40.14.0.13", {"position": v(601.71, 309.75) * mm});
            skLineSegment(sketch, "E40.direction1", {"start": v(311.71, 312.75) * mm, "end": v(331.71, 312.75) * mm, "construction": true});
            skArc(sketch, "E41.filletArc", {"start": v(321.71, 731.75) * mm, "mid": v(322.6, 729.63) * mm, "end": v(324.71, 728.75) * mm});
            skLineSegment(sketch, "E42", {"start": v(324.71, 728.75) * mm, "end": v(338.71, 728.75) * mm});
            skLineSegment(sketch, "E43.bottom", {"start": v(341.71, 728.75) * mm, "end": v(361.71, 728.75) * mm, "construction": true});
            skLineSegment(sketch, "E43.top", {"start": v(344.71, 747.75) * mm, "end": v(358.71, 747.75) * mm});
            skLineSegment(sketch, "E43.left", {"start": v(341.71, 731.75) * mm, "end": v(341.71, 744.75) * mm});
            skLineSegment(sketch, "E43.right", {"start": v(361.71, 728.75) * mm, "end": v(361.71, 744.75) * mm});
            skPoint(sketch, "E44.visualSharp", {"position": v(341.71, 747.75) * mm});
            skArc(sketch, "E44.filletArc", {"start": v(344.71, 747.75) * mm, "mid": v(342.6, 746.87) * mm, "end": v(341.71, 744.75) * mm});
            skPoint(sketch, "E45.visualSharp", {"position": v(361.71, 747.75) * mm});
            skArc(sketch, "E45.filletArc", {"start": v(361.71, 744.75) * mm, "mid": v(360.83, 746.87) * mm, "end": v(358.71, 747.75) * mm});
            skPoint(sketch, "E46.visualSharp", {"position": v(341.71, 728.75) * mm});
            skArc(sketch, "E46.filletArc", {"start": v(338.71, 728.75) * mm, "mid": v(340.83, 729.63) * mm, "end": v(341.71, 731.75) * mm});
            skLineSegment(sketch, "E47.1.0.0", {"start": v(361.71, 731.75) * mm, "end": v(361.71, 744.75) * mm});
            skLineSegment(sketch, "E47.1.0.1", {"start": v(364.71, 728.75) * mm, "end": v(378.71, 728.75) * mm});
            skLineSegment(sketch, "E47.1.0.2", {"start": v(381.71, 731.75) * mm, "end": v(381.71, 744.75) * mm});
            skLineSegment(sketch, "E47.1.0.3", {"start": v(384.71, 747.75) * mm, "end": v(398.71, 747.75) * mm});
            skArc(sketch, "E47.1.0.4", {"start": v(361.71, 731.75) * mm, "mid": v(362.6, 729.63) * mm, "end": v(364.71, 728.75) * mm});
            skArc(sketch, "E47.1.0.5", {"start": v(378.71, 728.75) * mm, "mid": v(380.83, 729.63) * mm, "end": v(381.71, 731.75) * mm});
            skArc(sketch, "E47.1.0.6", {"start": v(401.71, 744.75) * mm, "mid": v(400.83, 746.87) * mm, "end": v(398.71, 747.75) * mm});
            skArc(sketch, "E47.1.0.7", {"start": v(384.71, 747.75) * mm, "mid": v(382.6, 746.87) * mm, "end": v(381.71, 744.75) * mm});
            skPoint(sketch, "E47.1.0.8", {"position": v(381.71, 747.75) * mm});
            skPoint(sketch, "E47.1.0.9", {"position": v(401.71, 747.75) * mm});
            skPoint(sketch, "E47.1.0.10", {"position": v(381.71, 728.75) * mm});
            skLineSegment(sketch, "E47.2.0.0", {"start": v(401.71, 731.75) * mm, "end": v(401.71, 744.75) * mm});
            skLineSegment(sketch, "E47.2.0.1", {"start": v(404.71, 728.75) * mm, "end": v(418.71, 728.75) * mm});
            skLineSegment(sketch, "E47.2.0.2", {"start": v(421.71, 731.75) * mm, "end": v(421.71, 744.75) * mm});
            skLineSegment(sketch, "E47.2.0.3", {"start": v(424.71, 747.75) * mm, "end": v(438.71, 747.75) * mm});
            skArc(sketch, "E47.2.0.4", {"start": v(401.71, 731.75) * mm, "mid": v(402.6, 729.63) * mm, "end": v(404.71, 728.75) * mm});
            skArc(sketch, "E47.2.0.5", {"start": v(418.71, 728.75) * mm, "mid": v(420.83, 729.63) * mm, "end": v(421.71, 731.75) * mm});
            skArc(sketch, "E47.2.0.6", {"start": v(441.71, 744.75) * mm, "mid": v(440.83, 746.87) * mm, "end": v(438.71, 747.75) * mm});
            skArc(sketch, "E47.2.0.7", {"start": v(424.71, 747.75) * mm, "mid": v(422.6, 746.87) * mm, "end": v(421.71, 744.75) * mm});
            skPoint(sketch, "E47.2.0.8", {"position": v(421.71, 747.75) * mm});
            skPoint(sketch, "E47.2.0.9", {"position": v(441.71, 747.75) * mm});
            skPoint(sketch, "E47.2.0.10", {"position": v(421.71, 728.75) * mm});
            skLineSegment(sketch, "E47.3.0.0", {"start": v(441.71, 731.75) * mm, "end": v(441.71, 744.75) * mm});
            skLineSegment(sketch, "E47.3.0.1", {"start": v(444.71, 728.75) * mm, "end": v(458.71, 728.75) * mm});
            skLineSegment(sketch, "E47.3.0.2", {"start": v(461.71, 731.75) * mm, "end": v(461.71, 744.75) * mm});
            skLineSegment(sketch, "E47.3.0.3", {"start": v(464.71, 747.75) * mm, "end": v(478.71, 747.75) * mm});
            skArc(sketch, "E47.3.0.4", {"start": v(441.71, 731.75) * mm, "mid": v(442.6, 729.63) * mm, "end": v(444.71, 728.75) * mm});
            skArc(sketch, "E47.3.0.5", {"start": v(458.71, 728.75) * mm, "mid": v(460.83, 729.63) * mm, "end": v(461.71, 731.75) * mm});
            skArc(sketch, "E47.3.0.6", {"start": v(481.71, 744.75) * mm, "mid": v(480.83, 746.87) * mm, "end": v(478.71, 747.75) * mm});
            skArc(sketch, "E47.3.0.7", {"start": v(464.71, 747.75) * mm, "mid": v(462.6, 746.87) * mm, "end": v(461.71, 744.75) * mm});
            skPoint(sketch, "E47.3.0.8", {"position": v(461.71, 747.75) * mm});
            skPoint(sketch, "E47.3.0.9", {"position": v(481.71, 747.75) * mm});
            skPoint(sketch, "E47.3.0.10", {"position": v(461.71, 728.75) * mm});
            skLineSegment(sketch, "E47.4.0.0", {"start": v(481.71, 731.75) * mm, "end": v(481.71, 744.75) * mm});
            skLineSegment(sketch, "E47.4.0.1", {"start": v(484.71, 728.75) * mm, "end": v(498.71, 728.75) * mm});
            skLineSegment(sketch, "E47.4.0.2", {"start": v(501.71, 731.75) * mm, "end": v(501.71, 744.75) * mm});
            skLineSegment(sketch, "E47.4.0.3", {"start": v(504.71, 747.75) * mm, "end": v(518.71, 747.75) * mm});
            skArc(sketch, "E47.4.0.4", {"start": v(481.71, 731.75) * mm, "mid": v(482.6, 729.63) * mm, "end": v(484.71, 728.75) * mm});
            skArc(sketch, "E47.4.0.5", {"start": v(498.71, 728.75) * mm, "mid": v(500.83, 729.63) * mm, "end": v(501.71, 731.75) * mm});
            skArc(sketch, "E47.4.0.6", {"start": v(521.71, 744.75) * mm, "mid": v(520.83, 746.87) * mm, "end": v(518.71, 747.75) * mm});
            skArc(sketch, "E47.4.0.7", {"start": v(504.71, 747.75) * mm, "mid": v(502.6, 746.87) * mm, "end": v(501.71, 744.75) * mm});
            skPoint(sketch, "E47.4.0.8", {"position": v(501.71, 747.75) * mm});
            skPoint(sketch, "E47.4.0.9", {"position": v(521.71, 747.75) * mm});
            skPoint(sketch, "E47.4.0.10", {"position": v(501.71, 728.75) * mm});
            skLineSegment(sketch, "E47.5.0.0", {"start": v(521.71, 731.75) * mm, "end": v(521.71, 744.75) * mm});
            skLineSegment(sketch, "E47.5.0.1", {"start": v(524.71, 728.75) * mm, "end": v(538.71, 728.75) * mm});
            skLineSegment(sketch, "E47.5.0.2", {"start": v(541.71, 731.75) * mm, "end": v(541.71, 744.75) * mm});
            skLineSegment(sketch, "E47.5.0.3", {"start": v(544.71, 747.75) * mm, "end": v(558.71, 747.75) * mm});
            skArc(sketch, "E47.5.0.4", {"start": v(521.71, 731.75) * mm, "mid": v(522.6, 729.63) * mm, "end": v(524.71, 728.75) * mm});
            skArc(sketch, "E47.5.0.5", {"start": v(538.71, 728.75) * mm, "mid": v(540.83, 729.63) * mm, "end": v(541.71, 731.75) * mm});
            skArc(sketch, "E47.5.0.6", {"start": v(561.71, 744.75) * mm, "mid": v(560.83, 746.87) * mm, "end": v(558.71, 747.75) * mm});
            skArc(sketch, "E47.5.0.7", {"start": v(544.71, 747.75) * mm, "mid": v(542.6, 746.87) * mm, "end": v(541.71, 744.75) * mm});
            skPoint(sketch, "E47.5.0.8", {"position": v(541.71, 747.75) * mm});
            skPoint(sketch, "E47.5.0.9", {"position": v(561.71, 747.75) * mm});
            skPoint(sketch, "E47.5.0.10", {"position": v(541.71, 728.75) * mm});
            skLineSegment(sketch, "E47.6.0.0", {"start": v(561.71, 731.75) * mm, "end": v(561.71, 744.75) * mm});
            skLineSegment(sketch, "E47.6.0.1", {"start": v(564.71, 728.75) * mm, "end": v(578.71, 728.75) * mm});
            skLineSegment(sketch, "E47.6.0.2", {"start": v(581.71, 731.75) * mm, "end": v(581.71, 744.75) * mm});
            skLineSegment(sketch, "E47.6.0.3", {"start": v(584.71, 747.75) * mm, "end": v(598.71, 747.75) * mm});
            skArc(sketch, "E47.6.0.4", {"start": v(561.71, 731.75) * mm, "mid": v(562.6, 729.63) * mm, "end": v(564.71, 728.75) * mm});
            skArc(sketch, "E47.6.0.5", {"start": v(578.71, 728.75) * mm, "mid": v(580.83, 729.63) * mm, "end": v(581.71, 731.75) * mm});
            skArc(sketch, "E47.6.0.6", {"start": v(601.71, 744.75) * mm, "mid": v(600.83, 746.87) * mm, "end": v(598.71, 747.75) * mm});
            skArc(sketch, "E47.6.0.7", {"start": v(584.71, 747.75) * mm, "mid": v(582.6, 746.87) * mm, "end": v(581.71, 744.75) * mm});
            skPoint(sketch, "E47.6.0.8", {"position": v(581.71, 747.75) * mm});
            skPoint(sketch, "E47.6.0.9", {"position": v(601.71, 747.75) * mm});
            skPoint(sketch, "E47.6.0.10", {"position": v(581.71, 728.75) * mm});
            skLineSegment(sketch, "E48", {"start": v(601.71, 744.75) * mm, "end": v(601.71, 728.75) * mm});
            skLineSegment(sketch, "E49.bottom", {"start": v(301.71, 728.75) * mm, "end": v(601.71, 728.75) * mm, "construction": true});
            skLineSegment(sketch, "E49.top", {"start": v(301.71, 328.75) * mm, "end": v(601.71, 328.75) * mm, "construction": true});
            skLineSegment(sketch, "E49.left", {"start": v(301.71, 728.75) * mm, "end": v(301.71, 328.75) * mm, "construction": true});
            skLineSegment(sketch, "E49.right", {"start": v(601.71, 728.75) * mm, "end": v(601.71, 328.75) * mm, "construction": true});
            skLineSegment(sketch, "E50", {"start": v(301.71, 328.75) * mm, "end": v(282.71, 328.75) * mm});
            skLineSegment(sketch, "E51", {"start": v(282.71, 375.75) * mm, "end": v(282.71, 328.75) * mm});
            skLineSegment(sketch, "E52.bottom", {"start": v(282.71, 328.75) * mm, "end": v(311.71, 328.75) * mm});
            skLineSegment(sketch, "E52.top", {"start": v(282.71, 309.75) * mm, "end": v(308.71, 309.75) * mm});
            skLineSegment(sketch, "E52.left", {"start": v(282.71, 328.75) * mm, "end": v(282.71, 309.75) * mm});
            skLineSegment(sketch, "E53", {"start": v(311.71, 312.75) * mm, "end": v(311.71, 312.75) * mm});
            skLineSegment(sketch, "E54.bottom", {"start": v(302.21, 314.75) * mm, "end": v(289.21, 314.75) * mm});
            skLineSegment(sketch, "E54.top", {"start": v(302.21, 323.75) * mm, "end": v(289.21, 323.75) * mm});
            skLineSegment(sketch, "E54.left", {"start": v(305.21, 317.75) * mm, "end": v(305.21, 320.75) * mm});
            skLineSegment(sketch, "E54.right", {"start": v(286.21, 317.75) * mm, "end": v(286.21, 320.75) * mm});
            skPoint(sketch, "E54.middle", {"position": v(295.71, 319.25) * mm});
            skPoint(sketch, "E55.visualSharp", {"position": v(305.21, 323.75) * mm});
            skArc(sketch, "E55.filletArc", {"start": v(305.21, 320.75) * mm, "mid": v(304.33, 322.87) * mm, "end": v(302.21, 323.75) * mm});
            skPoint(sketch, "E56.visualSharp", {"position": v(305.21, 314.75) * mm});
            skArc(sketch, "E56.filletArc", {"start": v(302.21, 314.75) * mm, "mid": v(304.33, 315.63) * mm, "end": v(305.21, 317.75) * mm});
            skPoint(sketch, "E57.visualSharp", {"position": v(286.21, 314.75) * mm});
            skArc(sketch, "E57.filletArc", {"start": v(286.21, 317.75) * mm, "mid": v(287.1, 315.63) * mm, "end": v(289.21, 314.75) * mm});
            skPoint(sketch, "E58.visualSharp", {"position": v(286.21, 323.75) * mm});
            skArc(sketch, "E58.filletArc", {"start": v(289.21, 323.75) * mm, "mid": v(287.1, 322.87) * mm, "end": v(286.21, 320.75) * mm});
            skPoint(sketch, "E59.positionSnap0", {"position": v(295.71, 309.75) * mm});
            skPoint(sketch, "E59.positionSnap1", {"position": v(282.71, 319.25) * mm});
            skLineSegment(sketch, "E60", {"start": v(308.71, 309.75) * mm, "end": v(311.71, 309.75) * mm});
            skLineSegment(sketch, "E61", {"start": v(311.7, 309.8) * mm, "end": v(311.71, 312.75) * mm});
            skLineSegment(sketch, "E62", {"start": v(314.67, 309.76) * mm, "end": v(311.71, 309.75) * mm});
            skLineSegment(sketch, "E63", {"start": v(311.71, 309.75) * mm, "end": v(311.71, 325.75) * mm});
            skLineSegment(sketch, "E64", {"start": v(314.71, 309.75) * mm, "end": v(311.71, 309.75) * mm});
            skLineSegment(sketch, "E65", {"start": v(295.71, 323.75) * mm, "end": v(295.71, 319.25) * mm, "construction": true});
            skLineSegment(sketch, "E66", {"start": v(295.71, 319.25) * mm, "end": v(295.71, 314.75) * mm, "construction": true});
            skArc(sketch, "E67", {"start": v(295.71, 319.25) * mm, "mid": v(293.46, 317) * mm, "end": v(295.71, 314.75) * mm});
            skArc(sketch, "E68", {"start": v(295.71, 323.75) * mm, "mid": v(297.96, 321.5) * mm, "end": v(295.71, 319.25) * mm});
            skSolve(sketch);
        }
        {
            var Q0;
            Q0=qCreatedBy(makeId("Top.planeOp"),FACE);
            var sketch = newSketch(context, id + "F3", { "sketchPlane" : qUnion([Q0])});
            skLineSegment(sketch, "E69.bottom", {"start": v(355, 285) * mm, "end": v(655, 285) * mm, "construction": true});
            skLineSegment(sketch, "E69.top", {"start": v(355, 85) * mm, "end": v(655, 85) * mm, "construction": true});
            skLineSegment(sketch, "E69.left", {"start": v(355, 285) * mm, "end": v(355, 85) * mm, "construction": true});
            skLineSegment(sketch, "E69.right", {"start": v(655, 285) * mm, "end": v(655, 85) * mm, "construction": true});
            skLineSegment(sketch, "E70.bottom", {"start": v(655, 85) * mm, "end": v(855, 85) * mm, "construction": true});
            skLineSegment(sketch, "E70.top", {"start": v(655, 685) * mm, "end": v(855, 685) * mm, "construction": true});
            skLineSegment(sketch, "E70.left", {"start": v(655, 85) * mm, "end": v(655, 685) * mm, "construction": true});
            skLineSegment(sketch, "E70.right", {"start": v(855, 85) * mm, "end": v(855, 685) * mm, "construction": true});
            skPoint(sketch, "E71", {"position": v(855, 85) * mm});
            skSolve(sketch);
        }
        {
            var Q0;
            Q0=qCreatedBy(makeId("Top.planeOp"),FACE);
            var sketch = newSketch(context, id + "F4", { "sketchPlane" : qUnion([Q0])});
            skLineSegment(sketch, "E72.bottom", {"start": v(685, 295) * mm, "end": v(685, 295) * mm});
            skLineSegment(sketch, "E72.top", {"start": v(652, 295) * mm, "end": v(648, 295) * mm});
            skLineSegment(sketch, "E73.top", {"start": v(642, 304) * mm, "end": v(638, 304) * mm});
            skLineSegment(sketch, "E73.left", {"start": v(645, 298) * mm, "end": v(645, 301) * mm});
            skPoint(sketch, "E74.visualSharp", {"position": v(635, 304) * mm});
            skArc(sketch, "E74.filletArc", {"start": v(638, 304) * mm, "mid": v(635.88, 303.12) * mm, "end": v(635, 301) * mm});
            skPoint(sketch, "E75.visualSharp", {"position": v(655, 285) * mm});
            skPoint(sketch, "E76.visualSharp", {"position": v(645, 304) * mm});
            skArc(sketch, "E76.filletArc", {"start": v(645, 301) * mm, "mid": v(644.12, 303.12) * mm, "end": v(642, 304) * mm});
            skArc(sketch, "E77.filletArc", {"start": v(645, 298) * mm, "mid": v(645.88, 295.88) * mm, "end": v(648, 295) * mm});
            skArc(sketch, "E78.filletArc", {"start": v(652, 295) * mm, "mid": v(654.12, 295.88) * mm, "end": v(655, 298) * mm});
            skLineSegment(sketch, "E79", {"start": v(628, 285) * mm, "end": v(632, 285) * mm});
            skPoint(sketch, "E80.endSnap0", {"position": v(640, 304) * mm});
            skPoint(sketch, "E81.visualSharp", {"position": v(645, 285) * mm});
            skArc(sketch, "E81.filletArc", {"start": v(625, 288) * mm, "mid": v(625.88, 285.88) * mm, "end": v(628, 285) * mm});
            skArc(sketch, "E82.filletArc", {"start": v(632, 285) * mm, "mid": v(634.12, 285.88) * mm, "end": v(635, 288) * mm});
            skLineSegment(sketch, "E83", {"start": v(635, 301) * mm, "end": v(635, 288) * mm});
            skLineSegment(sketch, "E84", {"start": v(625, 288) * mm, "end": v(625, 301) * mm});
            skLineSegment(sketch, "E85", {"start": v(622, 304) * mm, "end": v(618, 304) * mm});
            skPoint(sketch, "E86.visualSharp", {"position": v(625, 304) * mm});
            skArc(sketch, "E86.filletArc", {"start": v(625, 301) * mm, "mid": v(624.12, 303.12) * mm, "end": v(622, 304) * mm});
            skPoint(sketch, "E87.visualSharp", {"position": v(615, 304) * mm});
            skArc(sketch, "E87.filletArc", {"start": v(618, 304) * mm, "mid": v(615.88, 303.12) * mm, "end": v(615, 301) * mm});
            skLineSegment(sketch, "E88.1.0.0", {"start": v(615, 301) * mm, "end": v(615, 288) * mm});
            skArc(sketch, "E88.1.0.1", {"start": v(598, 304) * mm, "mid": v(595.88, 303.12) * mm, "end": v(595, 301) * mm});
            skPoint(sketch, "E88.1.0.2", {"position": v(595, 304) * mm});
            skLineSegment(sketch, "E88.1.0.3", {"start": v(602, 304) * mm, "end": v(598, 304) * mm});
            skArc(sketch, "E88.1.0.4", {"start": v(605, 301) * mm, "mid": v(604.12, 303.12) * mm, "end": v(602, 304) * mm});
            skLineSegment(sketch, "E88.1.0.5", {"start": v(605, 288) * mm, "end": v(605, 301) * mm});
            skPoint(sketch, "E88.1.0.6", {"position": v(605, 304) * mm});
            skArc(sketch, "E88.1.0.7", {"start": v(605, 288) * mm, "mid": v(605.88, 285.88) * mm, "end": v(608, 285) * mm});
            skPoint(sketch, "E88.1.0.8", {"position": v(625, 285) * mm});
            skLineSegment(sketch, "E88.1.0.9", {"start": v(608, 285) * mm, "end": v(612, 285) * mm});
            skArc(sketch, "E88.1.0.10", {"start": v(612, 285) * mm, "mid": v(614.12, 285.88) * mm, "end": v(615, 288) * mm});
            skLineSegment(sketch, "E88.2.0.0", {"start": v(595, 301) * mm, "end": v(595, 288) * mm});
            skArc(sketch, "E88.2.0.1", {"start": v(578, 304) * mm, "mid": v(575.88, 303.12) * mm, "end": v(575, 301) * mm});
            skPoint(sketch, "E88.2.0.2", {"position": v(575, 304) * mm});
            skLineSegment(sketch, "E88.2.0.3", {"start": v(582, 304) * mm, "end": v(578, 304) * mm});
            skArc(sketch, "E88.2.0.4", {"start": v(585, 301) * mm, "mid": v(584.12, 303.12) * mm, "end": v(582, 304) * mm});
            skLineSegment(sketch, "E88.2.0.5", {"start": v(585, 288) * mm, "end": v(585, 301) * mm});
            skPoint(sketch, "E88.2.0.6", {"position": v(585, 304) * mm});
            skArc(sketch, "E88.2.0.7", {"start": v(585, 288) * mm, "mid": v(585.88, 285.88) * mm, "end": v(588, 285) * mm});
            skPoint(sketch, "E88.2.0.8", {"position": v(605, 285) * mm});
            skLineSegment(sketch, "E88.2.0.9", {"start": v(588, 285) * mm, "end": v(592, 285) * mm});
            skArc(sketch, "E88.2.0.10", {"start": v(592, 285) * mm, "mid": v(594.12, 285.88) * mm, "end": v(595, 288) * mm});
            skArc(sketch, "E88.2.0.11", {"start": v(598, 304) * mm, "mid": v(595.88, 303.12) * mm, "end": v(595, 301) * mm});
            skLineSegment(sketch, "E88.3.0.0", {"start": v(575, 301) * mm, "end": v(575, 288) * mm});
            skArc(sketch, "E88.3.0.1", {"start": v(558, 304) * mm, "mid": v(555.88, 303.12) * mm, "end": v(555, 301) * mm});
            skPoint(sketch, "E88.3.0.2", {"position": v(555, 304) * mm});
            skLineSegment(sketch, "E88.3.0.3", {"start": v(562, 304) * mm, "end": v(558, 304) * mm});
            skArc(sketch, "E88.3.0.4", {"start": v(565, 301) * mm, "mid": v(564.12, 303.12) * mm, "end": v(562, 304) * mm});
            skLineSegment(sketch, "E88.3.0.5", {"start": v(565, 288) * mm, "end": v(565, 301) * mm});
            skPoint(sketch, "E88.3.0.6", {"position": v(565, 304) * mm});
            skArc(sketch, "E88.3.0.7", {"start": v(565, 288) * mm, "mid": v(565.88, 285.88) * mm, "end": v(568, 285) * mm});
            skPoint(sketch, "E88.3.0.8", {"position": v(585, 285) * mm});
            skLineSegment(sketch, "E88.3.0.9", {"start": v(568, 285) * mm, "end": v(572, 285) * mm});
            skArc(sketch, "E88.3.0.10", {"start": v(572, 285) * mm, "mid": v(574.12, 285.88) * mm, "end": v(575, 288) * mm});
            skArc(sketch, "E88.3.0.11", {"start": v(578, 304) * mm, "mid": v(575.88, 303.12) * mm, "end": v(575, 301) * mm});
            skLineSegment(sketch, "E88.4.0.0", {"start": v(555, 301) * mm, "end": v(555, 288) * mm});
            skArc(sketch, "E88.4.0.1", {"start": v(538, 304) * mm, "mid": v(535.88, 303.12) * mm, "end": v(535, 301) * mm});
            skPoint(sketch, "E88.4.0.2", {"position": v(535, 304) * mm});
            skLineSegment(sketch, "E88.4.0.3", {"start": v(542, 304) * mm, "end": v(538, 304) * mm});
            skArc(sketch, "E88.4.0.4", {"start": v(545, 301) * mm, "mid": v(544.12, 303.12) * mm, "end": v(542, 304) * mm});
            skLineSegment(sketch, "E88.4.0.5", {"start": v(545, 288) * mm, "end": v(545, 301) * mm});
            skPoint(sketch, "E88.4.0.6", {"position": v(545, 304) * mm});
            skArc(sketch, "E88.4.0.7", {"start": v(545, 288) * mm, "mid": v(545.88, 285.88) * mm, "end": v(548, 285) * mm});
            skPoint(sketch, "E88.4.0.8", {"position": v(565, 285) * mm});
            skLineSegment(sketch, "E88.4.0.9", {"start": v(548, 285) * mm, "end": v(552, 285) * mm});
            skArc(sketch, "E88.4.0.10", {"start": v(552, 285) * mm, "mid": v(554.12, 285.88) * mm, "end": v(555, 288) * mm});
            skArc(sketch, "E88.4.0.11", {"start": v(558, 304) * mm, "mid": v(555.88, 303.12) * mm, "end": v(555, 301) * mm});
            skLineSegment(sketch, "E88.5.0.0", {"start": v(535, 301) * mm, "end": v(535, 288) * mm});
            skArc(sketch, "E88.5.0.1", {"start": v(518, 304) * mm, "mid": v(515.88, 303.12) * mm, "end": v(515, 301) * mm});
            skPoint(sketch, "E88.5.0.2", {"position": v(515, 304) * mm});
            skLineSegment(sketch, "E88.5.0.3", {"start": v(522, 304) * mm, "end": v(518, 304) * mm});
            skArc(sketch, "E88.5.0.4", {"start": v(525, 301) * mm, "mid": v(524.12, 303.12) * mm, "end": v(522, 304) * mm});
            skLineSegment(sketch, "E88.5.0.5", {"start": v(525, 288) * mm, "end": v(525, 301) * mm});
            skPoint(sketch, "E88.5.0.6", {"position": v(525, 304) * mm});
            skArc(sketch, "E88.5.0.7", {"start": v(525, 288) * mm, "mid": v(525.88, 285.88) * mm, "end": v(528, 285) * mm});
            skPoint(sketch, "E88.5.0.8", {"position": v(545, 285) * mm});
            skLineSegment(sketch, "E88.5.0.9", {"start": v(528, 285) * mm, "end": v(532, 285) * mm});
            skArc(sketch, "E88.5.0.10", {"start": v(532, 285) * mm, "mid": v(534.12, 285.88) * mm, "end": v(535, 288) * mm});
            skArc(sketch, "E88.5.0.11", {"start": v(538, 304) * mm, "mid": v(535.88, 303.12) * mm, "end": v(535, 301) * mm});
            skLineSegment(sketch, "E88.6.0.0", {"start": v(515, 301) * mm, "end": v(515, 288) * mm});
            skArc(sketch, "E88.6.0.1", {"start": v(498, 304) * mm, "mid": v(495.88, 303.12) * mm, "end": v(495, 301) * mm});
            skPoint(sketch, "E88.6.0.2", {"position": v(495, 304) * mm});
            skLineSegment(sketch, "E88.6.0.3", {"start": v(502, 304) * mm, "end": v(498, 304) * mm});
            skArc(sketch, "E88.6.0.4", {"start": v(505, 301) * mm, "mid": v(504.12, 303.12) * mm, "end": v(502, 304) * mm});
            skLineSegment(sketch, "E88.6.0.5", {"start": v(505, 288) * mm, "end": v(505, 301) * mm});
            skPoint(sketch, "E88.6.0.6", {"position": v(505, 304) * mm});
            skArc(sketch, "E88.6.0.7", {"start": v(505, 288) * mm, "mid": v(505.88, 285.88) * mm, "end": v(508, 285) * mm});
            skPoint(sketch, "E88.6.0.8", {"position": v(525, 285) * mm});
            skLineSegment(sketch, "E88.6.0.9", {"start": v(508, 285) * mm, "end": v(512, 285) * mm});
            skArc(sketch, "E88.6.0.10", {"start": v(512, 285) * mm, "mid": v(514.12, 285.88) * mm, "end": v(515, 288) * mm});
            skArc(sketch, "E88.6.0.11", {"start": v(518, 304) * mm, "mid": v(515.88, 303.12) * mm, "end": v(515, 301) * mm});
            skLineSegment(sketch, "E88.7.0.0", {"start": v(495, 301) * mm, "end": v(495, 288) * mm});
            skArc(sketch, "E88.7.0.1", {"start": v(478, 304) * mm, "mid": v(475.88, 303.12) * mm, "end": v(475, 301) * mm});
            skPoint(sketch, "E88.7.0.2", {"position": v(475, 304) * mm});
            skLineSegment(sketch, "E88.7.0.3", {"start": v(482, 304) * mm, "end": v(478, 304) * mm});
            skArc(sketch, "E88.7.0.4", {"start": v(485, 301) * mm, "mid": v(484.12, 303.12) * mm, "end": v(482, 304) * mm});
            skLineSegment(sketch, "E88.7.0.5", {"start": v(485, 288) * mm, "end": v(485, 301) * mm});
            skPoint(sketch, "E88.7.0.6", {"position": v(485, 304) * mm});
            skArc(sketch, "E88.7.0.7", {"start": v(485, 288) * mm, "mid": v(485.88, 285.88) * mm, "end": v(488, 285) * mm});
            skPoint(sketch, "E88.7.0.8", {"position": v(505, 285) * mm});
            skLineSegment(sketch, "E88.7.0.9", {"start": v(488, 285) * mm, "end": v(492, 285) * mm});
            skArc(sketch, "E88.7.0.10", {"start": v(492, 285) * mm, "mid": v(494.12, 285.88) * mm, "end": v(495, 288) * mm});
            skArc(sketch, "E88.7.0.11", {"start": v(498, 304) * mm, "mid": v(495.88, 303.12) * mm, "end": v(495, 301) * mm});
            skLineSegment(sketch, "E88.8.0.0", {"start": v(475, 301) * mm, "end": v(475, 288) * mm});
            skArc(sketch, "E88.8.0.1", {"start": v(458, 304) * mm, "mid": v(455.88, 303.12) * mm, "end": v(455, 301) * mm});
            skPoint(sketch, "E88.8.0.2", {"position": v(455, 304) * mm});
            skLineSegment(sketch, "E88.8.0.3", {"start": v(462, 304) * mm, "end": v(458, 304) * mm});
            skArc(sketch, "E88.8.0.4", {"start": v(465, 301) * mm, "mid": v(464.12, 303.12) * mm, "end": v(462, 304) * mm});
            skLineSegment(sketch, "E88.8.0.5", {"start": v(465, 288) * mm, "end": v(465, 301) * mm});
            skPoint(sketch, "E88.8.0.6", {"position": v(465, 304) * mm});
            skArc(sketch, "E88.8.0.7", {"start": v(465, 288) * mm, "mid": v(465.88, 285.88) * mm, "end": v(468, 285) * mm});
            skPoint(sketch, "E88.8.0.8", {"position": v(485, 285) * mm});
            skLineSegment(sketch, "E88.8.0.9", {"start": v(468, 285) * mm, "end": v(472, 285) * mm});
            skArc(sketch, "E88.8.0.10", {"start": v(472, 285) * mm, "mid": v(474.12, 285.88) * mm, "end": v(475, 288) * mm});
            skArc(sketch, "E88.8.0.11", {"start": v(478, 304) * mm, "mid": v(475.88, 303.12) * mm, "end": v(475, 301) * mm});
            skLineSegment(sketch, "E88.9.0.0", {"start": v(455, 301) * mm, "end": v(455, 288) * mm});
            skArc(sketch, "E88.9.0.1", {"start": v(438, 304) * mm, "mid": v(435.88, 303.12) * mm, "end": v(435, 301) * mm});
            skPoint(sketch, "E88.9.0.2", {"position": v(435, 304) * mm});
            skLineSegment(sketch, "E88.9.0.3", {"start": v(442, 304) * mm, "end": v(438, 304) * mm});
            skArc(sketch, "E88.9.0.4", {"start": v(445, 301) * mm, "mid": v(444.12, 303.12) * mm, "end": v(442, 304) * mm});
            skLineSegment(sketch, "E88.9.0.5", {"start": v(445, 288) * mm, "end": v(445, 301) * mm});
            skPoint(sketch, "E88.9.0.6", {"position": v(445, 304) * mm});
            skArc(sketch, "E88.9.0.7", {"start": v(445, 288) * mm, "mid": v(445.88, 285.88) * mm, "end": v(448, 285) * mm});
            skPoint(sketch, "E88.9.0.8", {"position": v(465, 285) * mm});
            skLineSegment(sketch, "E88.9.0.9", {"start": v(448, 285) * mm, "end": v(452, 285) * mm});
            skArc(sketch, "E88.9.0.10", {"start": v(452, 285) * mm, "mid": v(454.12, 285.88) * mm, "end": v(455, 288) * mm});
            skArc(sketch, "E88.9.0.11", {"start": v(458, 304) * mm, "mid": v(455.88, 303.12) * mm, "end": v(455, 301) * mm});
            skLineSegment(sketch, "E88.10.0.0", {"start": v(435, 301) * mm, "end": v(435, 288) * mm});
            skArc(sketch, "E88.10.0.1", {"start": v(418, 304) * mm, "mid": v(415.88, 303.12) * mm, "end": v(415, 301) * mm});
            skPoint(sketch, "E88.10.0.2", {"position": v(415, 304) * mm});
            skLineSegment(sketch, "E88.10.0.3", {"start": v(422, 304) * mm, "end": v(418, 304) * mm});
            skArc(sketch, "E88.10.0.4", {"start": v(425, 301) * mm, "mid": v(424.12, 303.12) * mm, "end": v(422, 304) * mm});
            skLineSegment(sketch, "E88.10.0.5", {"start": v(425, 288) * mm, "end": v(425, 301) * mm});
            skPoint(sketch, "E88.10.0.6", {"position": v(425, 304) * mm});
            skArc(sketch, "E88.10.0.7", {"start": v(425, 288) * mm, "mid": v(425.88, 285.88) * mm, "end": v(428, 285) * mm});
            skPoint(sketch, "E88.10.0.8", {"position": v(445, 285) * mm});
            skLineSegment(sketch, "E88.10.0.9", {"start": v(428, 285) * mm, "end": v(432, 285) * mm});
            skArc(sketch, "E88.10.0.10", {"start": v(432, 285) * mm, "mid": v(434.12, 285.88) * mm, "end": v(435, 288) * mm});
            skArc(sketch, "E88.10.0.11", {"start": v(438, 304) * mm, "mid": v(435.88, 303.12) * mm, "end": v(435, 301) * mm});
            skLineSegment(sketch, "E88.11.0.0", {"start": v(415, 301) * mm, "end": v(415, 288) * mm});
            skArc(sketch, "E88.11.0.1", {"start": v(398, 304) * mm, "mid": v(395.88, 303.12) * mm, "end": v(395, 301) * mm});
            skPoint(sketch, "E88.11.0.2", {"position": v(395, 304) * mm});
            skLineSegment(sketch, "E88.11.0.3", {"start": v(402, 304) * mm, "end": v(398, 304) * mm});
            skArc(sketch, "E88.11.0.4", {"start": v(405, 301) * mm, "mid": v(404.12, 303.12) * mm, "end": v(402, 304) * mm});
            skLineSegment(sketch, "E88.11.0.5", {"start": v(405, 288) * mm, "end": v(405, 301) * mm});
            skPoint(sketch, "E88.11.0.6", {"position": v(405, 304) * mm});
            skArc(sketch, "E88.11.0.7", {"start": v(405, 288) * mm, "mid": v(405.88, 285.88) * mm, "end": v(408, 285) * mm});
            skPoint(sketch, "E88.11.0.8", {"position": v(425, 285) * mm});
            skLineSegment(sketch, "E88.11.0.9", {"start": v(408, 285) * mm, "end": v(412, 285) * mm});
            skArc(sketch, "E88.11.0.10", {"start": v(412, 285) * mm, "mid": v(414.12, 285.88) * mm, "end": v(415, 288) * mm});
            skArc(sketch, "E88.11.0.11", {"start": v(418, 304) * mm, "mid": v(415.88, 303.12) * mm, "end": v(415, 301) * mm});
            skLineSegment(sketch, "E88.12.0.0", {"start": v(395, 301) * mm, "end": v(395, 288) * mm});
            skArc(sketch, "E88.12.0.1", {"start": v(378, 304) * mm, "mid": v(375.88, 303.12) * mm, "end": v(375, 301) * mm});
            skPoint(sketch, "E88.12.0.2", {"position": v(375, 304) * mm});
            skLineSegment(sketch, "E88.12.0.3", {"start": v(382, 304) * mm, "end": v(378, 304) * mm});
            skArc(sketch, "E88.12.0.4", {"start": v(385, 301) * mm, "mid": v(384.12, 303.12) * mm, "end": v(382, 304) * mm});
            skLineSegment(sketch, "E88.12.0.5", {"start": v(385, 288) * mm, "end": v(385, 301) * mm});
            skPoint(sketch, "E88.12.0.6", {"position": v(385, 304) * mm});
            skArc(sketch, "E88.12.0.7", {"start": v(385, 288) * mm, "mid": v(385.88, 285.88) * mm, "end": v(388, 285) * mm});
            skPoint(sketch, "E88.12.0.8", {"position": v(405, 285) * mm});
            skLineSegment(sketch, "E88.12.0.9", {"start": v(388, 285) * mm, "end": v(392, 285) * mm});
            skArc(sketch, "E88.12.0.10", {"start": v(392, 285) * mm, "mid": v(394.12, 285.88) * mm, "end": v(395, 288) * mm});
            skArc(sketch, "E88.12.0.11", {"start": v(398, 304) * mm, "mid": v(395.88, 303.12) * mm, "end": v(395, 301) * mm});
            skLineSegment(sketch, "E88.13.0.0", {"start": v(375, 301) * mm, "end": v(375, 288) * mm});
            skPoint(sketch, "E88.13.0.2", {"position": v(355, 304) * mm});
            skArc(sketch, "E88.13.0.4", {"start": v(365, 301) * mm, "mid": v(364.12, 303.12) * mm, "end": v(362, 304) * mm});
            skLineSegment(sketch, "E88.13.0.5", {"start": v(365, 288) * mm, "end": v(365, 301) * mm});
            skPoint(sketch, "E88.13.0.6", {"position": v(365, 304) * mm});
            skArc(sketch, "E88.13.0.7", {"start": v(365, 288) * mm, "mid": v(365.88, 285.88) * mm, "end": v(368, 285) * mm});
            skPoint(sketch, "E88.13.0.8", {"position": v(385, 285) * mm});
            skLineSegment(sketch, "E88.13.0.9", {"start": v(368, 285) * mm, "end": v(372, 285) * mm});
            skArc(sketch, "E88.13.0.10", {"start": v(372, 285) * mm, "mid": v(374.12, 285.88) * mm, "end": v(375, 288) * mm});
            skArc(sketch, "E88.13.0.11", {"start": v(378, 304) * mm, "mid": v(375.88, 303.12) * mm, "end": v(375, 301) * mm});
            skLineSegment(sketch, "E88.direction1", {"start": v(635, 288) * mm, "end": v(615, 288) * mm, "construction": true});
            skLineSegment(sketch, "E89", {"start": v(855, 85) * mm, "end": v(855, 685) * mm});
            skLineSegment(sketch, "E90", {"start": v(855, 685) * mm, "end": v(645, 685) * mm});
            skLineSegment(sketch, "E91", {"start": v(355, 281.4) * mm, "end": v(355, 160.07) * mm, "construction": true});
            skPoint(sketch, "E92.oppositeSnap0", {"position": v(360, 304) * mm});
            skLineSegment(sketch, "E93", {"start": v(316, 285) * mm, "end": v(316, 85) * mm});
            skLineSegment(sketch, "E94", {"start": v(316, 85) * mm, "end": v(855, 85) * mm});
            skLineSegment(sketch, "E95", {"start": v(655, 298) * mm, "end": v(655, 345) * mm});
            skLineSegment(sketch, "E96", {"start": v(635, 288) * mm, "end": v(635, 85) * mm});
            skLineSegment(sketch, "E97", {"start": v(655, 298) * mm, "end": v(655, 85) * mm});
            skLineSegment(sketch, "E98", {"start": v(362, 304) * mm, "end": v(358, 304) * mm});
            skLineSegment(sketch, "E99", {"start": v(355, 288) * mm, "end": v(355, 301) * mm});
            skLineSegment(sketch, "E100.bottom", {"start": v(335.5, 299) * mm, "end": v(322.5, 299) * mm});
            skLineSegment(sketch, "E100.top", {"start": v(335.5, 290) * mm, "end": v(322.5, 290) * mm});
            skLineSegment(sketch, "E100.left", {"start": v(338.5, 296) * mm, "end": v(338.5, 293) * mm});
            skLineSegment(sketch, "E100.right", {"start": v(319.5, 296) * mm, "end": v(319.5, 293) * mm});
            skPoint(sketch, "E100.middle", {"position": v(329, 294.5) * mm});
            skPoint(sketch, "E101.visualSharp", {"position": v(319.5, 299) * mm});
            skArc(sketch, "E101.filletArc", {"start": v(322.5, 299) * mm, "mid": v(320.38, 298.12) * mm, "end": v(319.5, 296) * mm});
            skPoint(sketch, "E102.visualSharp", {"position": v(319.5, 290) * mm});
            skArc(sketch, "E102.filletArc", {"start": v(319.5, 293) * mm, "mid": v(320.38, 290.88) * mm, "end": v(322.5, 290) * mm});
            skPoint(sketch, "E103.visualSharp", {"position": v(338.5, 299) * mm});
            skArc(sketch, "E103.filletArc", {"start": v(338.5, 296) * mm, "mid": v(337.62, 298.12) * mm, "end": v(335.5, 299) * mm});
            skPoint(sketch, "E104.visualSharp", {"position": v(338.5, 290) * mm});
            skArc(sketch, "E104.filletArc", {"start": v(335.5, 290) * mm, "mid": v(337.62, 290.88) * mm, "end": v(338.5, 293) * mm});
            skLineSegment(sketch, "E105", {"start": v(316, 285) * mm, "end": v(316, 304) * mm});
            skArc(sketch, "E106.filletArc", {"start": v(358, 304) * mm, "mid": v(355.88, 303.12) * mm, "end": v(355, 301) * mm});
            skLineSegment(sketch, "E107", {"start": v(352, 285) * mm, "end": v(348, 285) * mm});
            skLineSegment(sketch, "E108", {"start": v(345, 288) * mm, "end": v(345, 304) * mm});
            skLineSegment(sketch, "E109", {"start": v(342, 304) * mm, "end": v(316, 304) * mm});
            skPoint(sketch, "E110.visualSharp", {"position": v(345, 285) * mm});
            skLineSegment(sketch, "E111", {"start": v(316, 285) * mm, "end": v(348, 285) * mm});
            skLineSegment(sketch, "E112", {"start": v(345, 285) * mm, "end": v(345, 301) * mm});
            skPoint(sketch, "E113.visualSharp", {"position": v(355, 285) * mm});
            skArc(sketch, "E113.filletArc", {"start": v(352, 285) * mm, "mid": v(354.12, 285.88) * mm, "end": v(355, 288) * mm});
            skPoint(sketch, "E114.visualSharp", {"position": v(345, 304) * mm});
            skArc(sketch, "E114.filletArc", {"start": v(345, 301) * mm, "mid": v(344.12, 303.12) * mm, "end": v(342, 304) * mm});
            skPoint(sketch, "E115.centerSnap0", {"position": v(328.37, 296.75) * mm});
            skPoint(sketch, "E116.centerSnap0", {"position": v(329.9, 292.25) * mm});
            skArc(sketch, "E117", {"start": v(329, 294.5) * mm, "mid": v(326.75, 292.25) * mm, "end": v(329, 290) * mm});
            skArc(sketch, "E118", {"start": v(329, 299) * mm, "mid": v(331.25, 296.75) * mm, "end": v(329, 294.5) * mm});
            skSolve(sketch);
        }
        {
            var Q0;
            Q0=makeQuery(id+"F2.imprint","IMPRINT",FACE,{"disambiguationData":[TD([[makeQuery(id+"F2.imprint","IMPRINT",EDGE,{"derivedFrom":sQuery(id+"F2.wireOp",EDGE,"E4.left")}),-1.0]])]});
            var Q1;
            Q1=makeQuery(id+"F2.imprint","IMPRINT",FACE,{"disambiguationData":[TD([[makeQuery(id+"F2.imprint","IMPRINT",EDGE,{"derivedFrom":sQuery(id+"F2.wireOp",EDGE,"E54.right")}),-1.0]])]});
            var Q2;
            Q2=makeQuery(id+"F4.imprint","IMPRINT",FACE,{"disambiguationData":[TD([[makeQuery(id+"F4.imprint","IMPRINT",EDGE,{"derivedFrom":sQuery(id+"F4.wireOp",EDGE,"E79")}),-1.0]])]});
            var Q3;
            Q3=makeQuery(id+"F4.imprint","IMPRINT",FACE,{"disambiguationData":[TD([[makeQuery(id+"F4.imprint","IMPRINT",EDGE,{"derivedFrom":sQuery(id+"F4.wireOp",EDGE,"E100.left")}),-1.0]])]});
            var Q4;
            Q4=makeQuery(id+"F4.imprint","IMPRINT",FACE,{"disambiguationData":[TD([[makeQuery(id+"F4.imprint","IMPRINT",EDGE,{"derivedFrom":sQuery(id+"F4.wireOp",EDGE,"E72.top")}),1.0]])]});
            extrude(context, id + "F5", {"entities" : qUnion([Q0, Q1, Q2, Q3, Q4]), "depth" : 18 * mm});
        }
        {
            var Q0;
            {var subQ7=sQuery(id+"F2.wireOp",EDGE,"E35.filletArc");Q0=makeQuery(id+"F2.imprint","IMPRINT",FACE,{"disambiguationData":[TD([[makeQuery(id+"F2.imprint","IMPRINT",EDGE,{"derivedFrom":subQ7}),1.0]])]});}
            extrude(context, id + "F6", {"entities" : qUnion([Q0]), "depth" : 9 * mm});
        }
        {
            var Q0;
            Q0=makeQuery(id+"F4.imprint","IMPRINT",FACE,{"disambiguationData":[TD([[makeQuery(id+"F4.imprint","IMPRINT",EDGE,{"derivedFrom":sQuery(id+"F4.wireOp",EDGE,"E100.left")}),1.0]])]});
            extrude(context, id + "F7", {"entities" : qUnion([Q0]), "depth" : 18 * mm, "hasSecondDirection" : true, "secondDirectionOppositeDirection" : false, "secondDirectionDepth" : 9 * mm});
        }
    });
